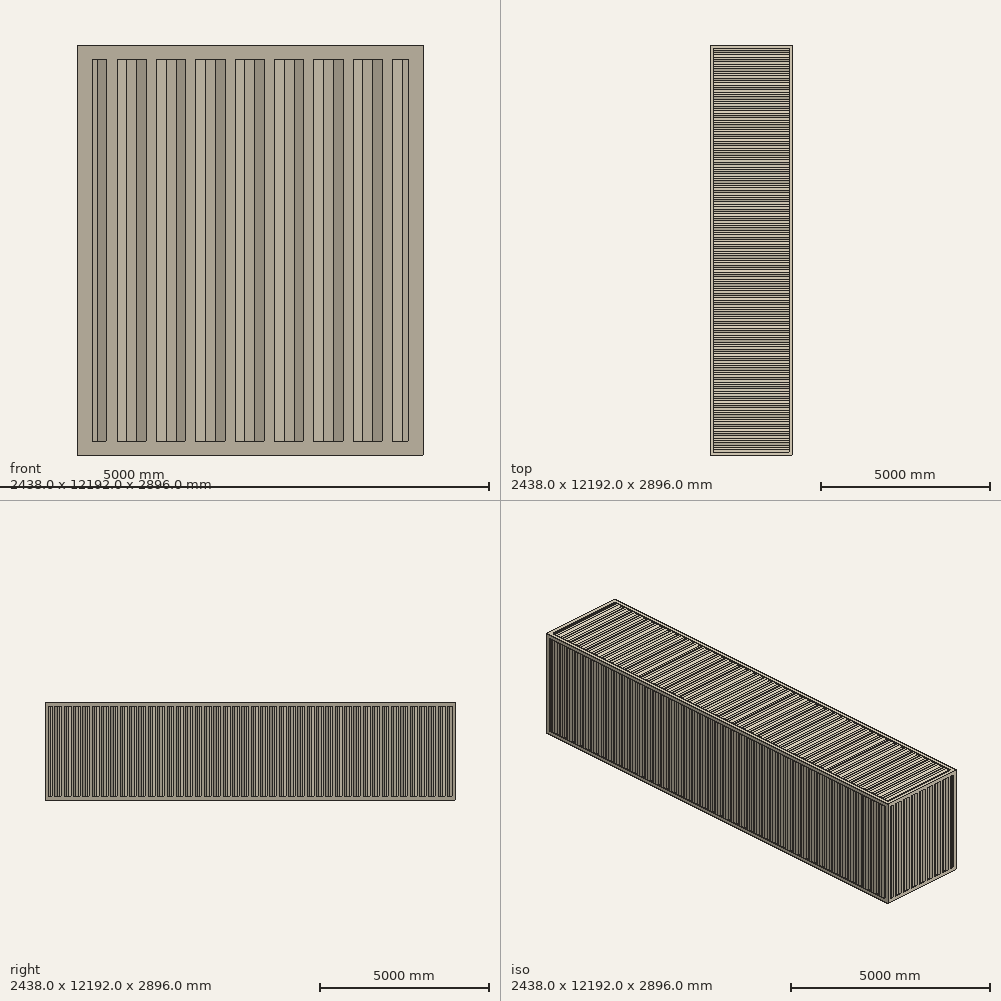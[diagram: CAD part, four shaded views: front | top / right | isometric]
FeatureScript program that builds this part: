
annotation { "Feature Type Name" : "Feature", "Feature Type Description" : "" }
export const myFeature = defineFeature(function(context is Context, id is Id, definition is map)
    precondition{}
    {
        {
            var Q0;
            Q0=qCreatedBy(makeId("Top.planeOp"),FACE);
            var sketch = newSketch(context, id + "F0", { "sketchPlane" : qUnion([Q0])});
            skLineSegment(sketch, "E0.bottom", {"start": v(0, 0) * mm, "end": v(-2438, 0) * mm});
            skLineSegment(sketch, "E0.top", {"start": v(0, 12192) * mm, "end": v(-2438, 12192) * mm});
            skLineSegment(sketch, "E0.left", {"start": v(0, 0) * mm, "end": v(0, 12192) * mm});
            skLineSegment(sketch, "E0.right", {"start": v(-2438, 0) * mm, "end": v(-2438, 12192) * mm});
            skSolve(sketch);
        }
        {
            var Q0;
            Q0 = qSketchRegion(id + "F0", true);
            extrude(context, id + "F1", {"entities" : qUnion([Q0]), "depth" : 2896 * mm, "offsetDistance" : 25 * mm});
        }
        {
            var Q0;
            Q0=makeQuery(id+"F1.opExtrude","SWEPT_FACE",FACE,{"disambiguationData":[OSD([sQuery(id+"F0.wireOp",EDGE,"E0.bottom")])]});
            var sketch = newSketch(context, id + "F2", { "sketchPlane" : qUnion([Q0])});
            skLineSegment(sketch, "E1", {"start": v(-2438, 2896) * mm, "end": v(-2338, 2896) * mm});
            skLineSegment(sketch, "E2", {"start": v(-2338, 2896) * mm, "end": v(-2338, 100) * mm});
            skLineSegment(sketch, "E3", {"start": v(-2338, 100) * mm, "end": v(-100, 100) * mm});
            skLineSegment(sketch, "E4", {"start": v(-100, 100) * mm, "end": v(-100, 2796) * mm});
            skLineSegment(sketch, "E5", {"start": v(-100, 2796) * mm, "end": v(-2338, 2796) * mm});
            skSolve(sketch);
        }
        {
            var Q0;
            Q0 = qSketchRegion(id + "F2", true);
            extrude(context, id + "F3", {"entities" : qUnion([Q0]), "operationType" : NewBodyOperationType.REMOVE, "oppositeDirection" : true, "depth" : 12192 * mm, "offsetDistance" : 25 * mm});
        }
        {
            var Q0;
            Q0=makeQuery(id+"F1.opExtrude","SWEPT_FACE",FACE,{"disambiguationData":[OSD([sQuery(id+"F0.wireOp",EDGE,"E0.left")])]});
            var sketch = newSketch(context, id + "F4", { "sketchPlane" : qUnion([Q0])});
            skLineSegment(sketch, "E6", {"start": v(0, 2896) * mm, "end": v(100, 2896) * mm});
            skLineSegment(sketch, "E7", {"start": v(100, 2896) * mm, "end": v(100, 100) * mm});
            skLineSegment(sketch, "E8", {"start": v(100, 100) * mm, "end": v(12092, 100) * mm});
            skLineSegment(sketch, "E9", {"start": v(12092, 100) * mm, "end": v(12092, 2796) * mm});
            skLineSegment(sketch, "E10", {"start": v(12092, 2796) * mm, "end": v(100, 2796) * mm});
            skSolve(sketch);
        }
        {
            var Q0;
            Q0 = qSketchRegion(id + "F4", true);
            extrude(context, id + "F5", {"entities" : qUnion([Q0]), "operationType" : NewBodyOperationType.REMOVE, "oppositeDirection" : true, "depth" : 2438 * mm, "offsetDistance" : 25 * mm});
        }
        {
            var Q0;
            Q0=makeQuery(id+"F1.opExtrude","CAP_FACE",FACE,{"disambiguationData":[OSD([sQuery(id+"F0.wireOp",EDGE,"E0.bottom"),sQuery(id+"F0.wireOp",EDGE,"E0.top"),sQuery(id+"F0.wireOp",EDGE,"E0.left"),sQuery(id+"F0.wireOp",EDGE,"E0.right")])],"isStart":false});
            var sketch = newSketch(context, id + "F6", { "sketchPlane" : qUnion([Q0])});
            skLineSegment(sketch, "E11", {"start": v(-2438, 0) * mm, "end": v(-2338, 0) * mm});
            skLineSegment(sketch, "E12", {"start": v(-2338, 0) * mm, "end": v(-2338, 12092) * mm});
            skLineSegment(sketch, "E13", {"start": v(-2338, 12092) * mm, "end": v(-100, 12092) * mm});
            skLineSegment(sketch, "E14", {"start": v(-100, 12092) * mm, "end": v(-100, 100) * mm});
            skLineSegment(sketch, "E15", {"start": v(-100, 100) * mm, "end": v(-2338, 100) * mm});
            skSolve(sketch);
        }
        {
            var Q0;
            Q0 = qSketchRegion(id + "F6", true);
            extrude(context, id + "F7", {"entities" : qUnion([Q0]), "operationType" : NewBodyOperationType.REMOVE, "oppositeDirection" : true, "depth" : 100 * mm, "offsetDistance" : 25 * mm});
        }
        {
            var Q0;
            Q0=makeQuery(id+"F5.boolean.opBoolean","MERGE",FACE,{"derivedFrom":[makeQuery(id+"F3.boolean.opBoolean","COPY",FACE,{"derivedFrom":makeQuery(id+"F3.opExtrude","SWEPT_FACE",FACE,{"disambiguationData":[OSD([sQuery(id+"F2.wireOp",EDGE,"E3")])]})})],"fromTools":[makeQuery(id+"F5.opExtrude","SWEPT_FACE",FACE,{"disambiguationData":[OSD([sQuery(id+"F4.wireOp",EDGE,"E8")])]})]});
            var sketch = newSketch(context, id + "F8", { "sketchPlane" : qUnion([Q0])});
            skLineSegment(sketch, "E16", {"start": v(-2338, 36) * mm, "end": v(-2301, 36) * mm});
            skLineSegment(sketch, "E17", {"start": v(-2233, 0) * mm, "end": v(-2161, 0) * mm});
            skLineSegment(sketch, "E18", {"start": v(-2093, 36) * mm, "end": v(-2023, 36) * mm});
            skLineSegment(sketch, "E19", {"start": v(-2301, 36) * mm, "end": v(-2233, 0) * mm});
            skLineSegment(sketch, "E20", {"start": v(-2161, 0) * mm, "end": v(-2093, 36) * mm});
            skLineSegment(sketch, "E21.1.0.0", {"start": v(-2023, 36) * mm, "end": v(-1955, 0) * mm});
            skLineSegment(sketch, "E21.1.0.1", {"start": v(-1955, 0) * mm, "end": v(-1883, 0) * mm});
            skLineSegment(sketch, "E21.1.0.2", {"start": v(-1883, 0) * mm, "end": v(-1815, 36) * mm});
            skLineSegment(sketch, "E21.1.0.3", {"start": v(-1815, 36) * mm, "end": v(-1745, 36) * mm});
            skLineSegment(sketch, "E21.2.0.0", {"start": v(-1745, 36) * mm, "end": v(-1677, 0) * mm});
            skLineSegment(sketch, "E21.2.0.1", {"start": v(-1677, 0) * mm, "end": v(-1605, 0) * mm});
            skLineSegment(sketch, "E21.2.0.2", {"start": v(-1605, 0) * mm, "end": v(-1537, 36) * mm});
            skLineSegment(sketch, "E21.2.0.3", {"start": v(-1537, 36) * mm, "end": v(-1467, 36) * mm});
            skLineSegment(sketch, "E21.3.0.0", {"start": v(-1467, 36) * mm, "end": v(-1399, 0) * mm});
            skLineSegment(sketch, "E21.3.0.1", {"start": v(-1399, 0) * mm, "end": v(-1327, 0) * mm});
            skLineSegment(sketch, "E21.3.0.2", {"start": v(-1327, 0) * mm, "end": v(-1259, 36) * mm});
            skLineSegment(sketch, "E21.3.0.3", {"start": v(-1259, 36) * mm, "end": v(-1189, 36) * mm});
            skLineSegment(sketch, "E21.4.0.0", {"start": v(-1189, 36) * mm, "end": v(-1121, 0) * mm});
            skLineSegment(sketch, "E21.4.0.1", {"start": v(-1121, 0) * mm, "end": v(-1049, 0) * mm});
            skLineSegment(sketch, "E21.4.0.2", {"start": v(-1049, 0) * mm, "end": v(-981, 36) * mm});
            skLineSegment(sketch, "E21.4.0.3", {"start": v(-981, 36) * mm, "end": v(-911, 36) * mm});
            skLineSegment(sketch, "E21.5.0.0", {"start": v(-911, 36) * mm, "end": v(-843, 0) * mm});
            skLineSegment(sketch, "E21.5.0.1", {"start": v(-843, 0) * mm, "end": v(-771, 0) * mm});
            skLineSegment(sketch, "E21.5.0.2", {"start": v(-771, 0) * mm, "end": v(-703, 36) * mm});
            skLineSegment(sketch, "E21.5.0.3", {"start": v(-703, 36) * mm, "end": v(-633, 36) * mm});
            skLineSegment(sketch, "E21.6.0.0", {"start": v(-633, 36) * mm, "end": v(-565, 0) * mm});
            skLineSegment(sketch, "E21.6.0.1", {"start": v(-565, 0) * mm, "end": v(-493, 0) * mm});
            skLineSegment(sketch, "E21.6.0.2", {"start": v(-493, 0) * mm, "end": v(-425, 36) * mm});
            skLineSegment(sketch, "E21.6.0.3", {"start": v(-425, 36) * mm, "end": v(-355, 36) * mm});
            skLineSegment(sketch, "E21.direction1", {"start": v(-2301, 36) * mm, "end": v(-2023, 36) * mm, "construction": true});
            skLineSegment(sketch, "E22.1.0.0", {"start": v(-355, 36) * mm, "end": v(-287, 0) * mm});
            skLineSegment(sketch, "E22.1.0.1", {"start": v(-287, 0) * mm, "end": v(-215, 0) * mm});
            skLineSegment(sketch, "E22.1.0.2", {"start": v(-215, 0) * mm, "end": v(-147, 36) * mm});
            skLineSegment(sketch, "E22.direction1", {"start": v(-633, 36) * mm, "end": v(-355, 36) * mm, "construction": true});
            skLineSegment(sketch, "E23", {"start": v(-147, 36) * mm, "end": v(-100, 36) * mm});
            skLineSegment(sketch, "E24.0.1.0", {"start": v(-2301, 37) * mm, "end": v(-2023, 37) * mm, "construction": true});
            skLineSegment(sketch, "E24.0.1.1", {"start": v(-633, 37) * mm, "end": v(-355, 37) * mm, "construction": true});
            skLineSegment(sketch, "E24.0.1.2", {"start": v(-355, 37) * mm, "end": v(-287, 1) * mm});
            skLineSegment(sketch, "E24.0.1.3", {"start": v(-1259, 37) * mm, "end": v(-1189, 37) * mm});
            skLineSegment(sketch, "E24.0.1.4", {"start": v(-147, 37) * mm, "end": v(-100, 37) * mm});
            skLineSegment(sketch, "E24.0.1.5", {"start": v(-1605, 1) * mm, "end": v(-1537, 37) * mm});
            skLineSegment(sketch, "E24.0.1.6", {"start": v(-1467, 37) * mm, "end": v(-1399, 1) * mm});
            skLineSegment(sketch, "E24.0.1.7", {"start": v(-1049, 1) * mm, "end": v(-981, 37) * mm});
            skLineSegment(sketch, "E24.0.1.8", {"start": v(-633, 37) * mm, "end": v(-565, 1) * mm});
            skLineSegment(sketch, "E24.0.1.9", {"start": v(-1955, 1) * mm, "end": v(-1883, 1) * mm});
            skLineSegment(sketch, "E24.0.1.10", {"start": v(-215, 1) * mm, "end": v(-147, 37) * mm});
            skLineSegment(sketch, "E24.0.1.11", {"start": v(-911, 37) * mm, "end": v(-843, 1) * mm});
            skLineSegment(sketch, "E24.0.1.12", {"start": v(-1883, 1) * mm, "end": v(-1815, 37) * mm});
            skLineSegment(sketch, "E24.0.1.13", {"start": v(-2023, 37) * mm, "end": v(-1955, 1) * mm});
            skLineSegment(sketch, "E24.0.1.14", {"start": v(-493, 1) * mm, "end": v(-425, 37) * mm});
            skLineSegment(sketch, "E24.0.1.15", {"start": v(-1677, 1) * mm, "end": v(-1605, 1) * mm});
            skLineSegment(sketch, "E24.0.1.16", {"start": v(-1189, 37) * mm, "end": v(-1121, 1) * mm});
            skLineSegment(sketch, "E24.0.1.17", {"start": v(-1745, 37) * mm, "end": v(-1677, 1) * mm});
            skLineSegment(sketch, "E24.0.1.18", {"start": v(-287, 1) * mm, "end": v(-215, 1) * mm});
            skLineSegment(sketch, "E24.0.1.19", {"start": v(-981, 37) * mm, "end": v(-911, 37) * mm});
            skLineSegment(sketch, "E24.0.1.20", {"start": v(-843, 1) * mm, "end": v(-771, 1) * mm});
            skLineSegment(sketch, "E24.0.1.21", {"start": v(-771, 1) * mm, "end": v(-703, 37) * mm});
            skLineSegment(sketch, "E24.0.1.22", {"start": v(-1815, 37) * mm, "end": v(-1745, 37) * mm});
            skLineSegment(sketch, "E24.0.1.23", {"start": v(-565, 1) * mm, "end": v(-493, 1) * mm});
            skLineSegment(sketch, "E24.0.1.24", {"start": v(-2161, 1) * mm, "end": v(-2093, 37) * mm});
            skLineSegment(sketch, "E24.0.1.25", {"start": v(-1121, 1) * mm, "end": v(-1049, 1) * mm});
            skLineSegment(sketch, "E24.0.1.26", {"start": v(-2301, 37) * mm, "end": v(-2233, 1) * mm});
            skLineSegment(sketch, "E24.0.1.27", {"start": v(-1537, 37) * mm, "end": v(-1467, 37) * mm});
            skLineSegment(sketch, "E24.0.1.28", {"start": v(-1399, 1) * mm, "end": v(-1327, 1) * mm});
            skLineSegment(sketch, "E24.0.1.29", {"start": v(-2233, 1) * mm, "end": v(-2161, 1) * mm});
            skLineSegment(sketch, "E24.0.1.30", {"start": v(-1327, 1) * mm, "end": v(-1259, 37) * mm});
            skLineSegment(sketch, "E24.0.1.31", {"start": v(-425, 37) * mm, "end": v(-355, 37) * mm});
            skLineSegment(sketch, "E24.0.1.32", {"start": v(-2093, 37) * mm, "end": v(-2023, 37) * mm});
            skLineSegment(sketch, "E24.0.1.33", {"start": v(-703, 37) * mm, "end": v(-633, 37) * mm});
            skLineSegment(sketch, "E24.0.1.34", {"start": v(-2338, 37) * mm, "end": v(-2301, 37) * mm});
            skLineSegment(sketch, "E24.direction1", {"start": v(-2338, 36) * mm, "end": v(-2313, 36) * mm, "construction": true});
            skLineSegment(sketch, "E24.direction2", {"start": v(-2338, 36) * mm, "end": v(-2338, 37) * mm, "construction": true});
            skLineSegment(sketch, "E25", {"start": v(-2338, 37) * mm, "end": v(-2338, 36) * mm});
            skLineSegment(sketch, "E26", {"start": v(-100, 37) * mm, "end": v(-100, 36) * mm});
            skSolve(sketch);
        }
        {
            var Q0;
            Q0 = qSketchRegion(id + "F8", true);
            extrude(context, id + "F9", {"entities" : qUnion([Q0]), "operationType" : NewBodyOperationType.ADD, "depth" : 2696 * mm, "offsetDistance" : 25 * mm});
        }
        {
            var Q0;
            {var subQ4=makeQuery(id+"F3.boolean.opBoolean","COPY",FACE,{"derivedFrom":makeQuery(id+"F3.opExtrude","SWEPT_FACE",FACE,{"disambiguationData":[OSD([sQuery(id+"F2.wireOp",EDGE,"E3")])]})});var subQ5=makeQuery(id+"F5.opExtrude","SWEPT_FACE",FACE,{"disambiguationData":[OSD([sQuery(id+"F4.wireOp",EDGE,"E8")])]});Q0=makeQuery(id+"F9.boolean.opBoolean","SPLIT",FACE,{"disambiguationData":[TD([makeQuery(id+"F1.opExtrude","SWEPT_FACE",FACE,{"disambiguationData":[OSD([sQuery(id+"F0.wireOp",EDGE,"E0.top")])]})])],"derivedFrom":makeQuery(id+"F5.boolean.opBoolean","MERGE",FACE,{"derivedFrom":[subQ4],"fromTools":[subQ5]})});}
            var sketch = newSketch(context, id + "F10", { "sketchPlane" : qUnion([Q0])});
            skLineSegment(sketch, "E27", {"start": v(-100, 12156) * mm, "end": v(-137, 12156) * mm});
            skLineSegment(sketch, "E28", {"start": v(-205.08, 12191.96) * mm, "end": v(-277.08, 12191.96) * mm});
            skLineSegment(sketch, "E29", {"start": v(-345, 12156) * mm, "end": v(-415, 12156) * mm});
            skLineSegment(sketch, "E30", {"start": v(-137, 12156) * mm, "end": v(-205.08, 12191.96) * mm});
            skLineSegment(sketch, "E31", {"start": v(-277.08, 12191.96) * mm, "end": v(-345, 12156) * mm});
            skLineSegment(sketch, "E32.1.0.0", {"start": v(-415, 12156) * mm, "end": v(-483.08, 12191.96) * mm});
            skLineSegment(sketch, "E32.1.0.1", {"start": v(-483.08, 12191.96) * mm, "end": v(-555.08, 12191.96) * mm});
            skLineSegment(sketch, "E32.1.0.2", {"start": v(-555.08, 12191.96) * mm, "end": v(-623, 12156) * mm});
            skLineSegment(sketch, "E32.1.0.3", {"start": v(-623, 12156) * mm, "end": v(-693, 12156) * mm});
            skLineSegment(sketch, "E32.2.0.0", {"start": v(-693, 12156) * mm, "end": v(-761.08, 12191.96) * mm});
            skLineSegment(sketch, "E32.2.0.1", {"start": v(-761.08, 12191.96) * mm, "end": v(-833.08, 12191.96) * mm});
            skLineSegment(sketch, "E32.2.0.2", {"start": v(-833.08, 12191.96) * mm, "end": v(-901, 12156) * mm});
            skLineSegment(sketch, "E32.2.0.3", {"start": v(-901, 12156) * mm, "end": v(-971, 12156) * mm});
            skLineSegment(sketch, "E32.3.0.0", {"start": v(-971, 12156) * mm, "end": v(-1039.08, 12191.96) * mm});
            skLineSegment(sketch, "E32.3.0.1", {"start": v(-1039.08, 12191.96) * mm, "end": v(-1111.08, 12191.96) * mm});
            skLineSegment(sketch, "E32.3.0.2", {"start": v(-1111.08, 12191.96) * mm, "end": v(-1179, 12156) * mm});
            skLineSegment(sketch, "E32.3.0.3", {"start": v(-1179, 12156) * mm, "end": v(-1249, 12156) * mm});
            skLineSegment(sketch, "E32.4.0.0", {"start": v(-1249, 12156) * mm, "end": v(-1317.08, 12191.96) * mm});
            skLineSegment(sketch, "E32.4.0.1", {"start": v(-1317.08, 12191.96) * mm, "end": v(-1389.08, 12191.96) * mm});
            skLineSegment(sketch, "E32.4.0.2", {"start": v(-1389.08, 12191.96) * mm, "end": v(-1457, 12156) * mm});
            skLineSegment(sketch, "E32.4.0.3", {"start": v(-1457, 12156) * mm, "end": v(-1527, 12156) * mm});
            skLineSegment(sketch, "E32.5.0.0", {"start": v(-1527, 12156) * mm, "end": v(-1595.08, 12191.96) * mm});
            skLineSegment(sketch, "E32.5.0.1", {"start": v(-1595.08, 12191.96) * mm, "end": v(-1667.08, 12191.96) * mm});
            skLineSegment(sketch, "E32.5.0.2", {"start": v(-1667.08, 12191.96) * mm, "end": v(-1735, 12156) * mm});
            skLineSegment(sketch, "E32.5.0.3", {"start": v(-1735, 12156) * mm, "end": v(-1805, 12156) * mm});
            skLineSegment(sketch, "E32.6.0.0", {"start": v(-1805, 12156) * mm, "end": v(-1873.08, 12191.96) * mm});
            skLineSegment(sketch, "E32.6.0.1", {"start": v(-1873.08, 12191.96) * mm, "end": v(-1945.08, 12191.96) * mm});
            skLineSegment(sketch, "E32.6.0.2", {"start": v(-1945.08, 12191.96) * mm, "end": v(-2013, 12156) * mm});
            skLineSegment(sketch, "E32.6.0.3", {"start": v(-2013, 12156) * mm, "end": v(-2083, 12156) * mm});
            skLineSegment(sketch, "E32.direction1", {"start": v(-137, 12156) * mm, "end": v(-415, 12156) * mm, "construction": true});
            skLineSegment(sketch, "E33.1.0.0", {"start": v(-2083, 12156) * mm, "end": v(-2151.08, 12191.96) * mm});
            skLineSegment(sketch, "E33.1.0.1", {"start": v(-2151.08, 12191.96) * mm, "end": v(-2223.08, 12191.96) * mm});
            skLineSegment(sketch, "E33.1.0.2", {"start": v(-2223.08, 12191.96) * mm, "end": v(-2291, 12156) * mm});
            skLineSegment(sketch, "E33.direction1", {"start": v(-1805, 12156) * mm, "end": v(-2083, 12156) * mm, "construction": true});
            skLineSegment(sketch, "E34", {"start": v(-2291, 12156) * mm, "end": v(-2338, 12156) * mm});
            skLineSegment(sketch, "E35.0.1.0", {"start": v(-137, 12155) * mm, "end": v(-415, 12155) * mm, "construction": true});
            skLineSegment(sketch, "E35.0.1.1", {"start": v(-1805, 12155) * mm, "end": v(-2083, 12155) * mm, "construction": true});
            skLineSegment(sketch, "E35.0.1.2", {"start": v(-2083, 12155) * mm, "end": v(-2151.08, 12190.96) * mm});
            skLineSegment(sketch, "E35.0.1.3", {"start": v(-1179, 12155) * mm, "end": v(-1249, 12155) * mm});
            skLineSegment(sketch, "E35.0.1.4", {"start": v(-2291, 12155) * mm, "end": v(-2338, 12155) * mm});
            skLineSegment(sketch, "E35.0.1.5", {"start": v(-833.08, 12190.96) * mm, "end": v(-901, 12155) * mm});
            skLineSegment(sketch, "E35.0.1.6", {"start": v(-971, 12155) * mm, "end": v(-1039.08, 12190.96) * mm});
            skLineSegment(sketch, "E35.0.1.7", {"start": v(-1389.08, 12190.96) * mm, "end": v(-1457, 12155) * mm});
            skLineSegment(sketch, "E35.0.1.8", {"start": v(-1805, 12155) * mm, "end": v(-1873.08, 12190.96) * mm});
            skLineSegment(sketch, "E35.0.1.9", {"start": v(-483.08, 12190.96) * mm, "end": v(-555.08, 12190.96) * mm});
            skLineSegment(sketch, "E35.0.1.10", {"start": v(-2223.08, 12190.96) * mm, "end": v(-2291, 12155) * mm});
            skLineSegment(sketch, "E35.0.1.11", {"start": v(-1527, 12155) * mm, "end": v(-1595.08, 12190.96) * mm});
            skLineSegment(sketch, "E35.0.1.12", {"start": v(-555.08, 12190.96) * mm, "end": v(-623, 12155) * mm});
            skLineSegment(sketch, "E35.0.1.13", {"start": v(-415, 12155) * mm, "end": v(-483.08, 12190.96) * mm});
            skLineSegment(sketch, "E35.0.1.14", {"start": v(-1945.08, 12190.96) * mm, "end": v(-2013, 12155) * mm});
            skLineSegment(sketch, "E35.0.1.15", {"start": v(-761.08, 12190.96) * mm, "end": v(-833.08, 12190.96) * mm});
            skLineSegment(sketch, "E35.0.1.16", {"start": v(-1249, 12155) * mm, "end": v(-1317.08, 12190.96) * mm});
            skLineSegment(sketch, "E35.0.1.17", {"start": v(-693, 12155) * mm, "end": v(-761.08, 12190.96) * mm});
            skLineSegment(sketch, "E35.0.1.18", {"start": v(-2151.08, 12190.96) * mm, "end": v(-2223.08, 12190.96) * mm});
            skLineSegment(sketch, "E35.0.1.19", {"start": v(-1457, 12155) * mm, "end": v(-1527, 12155) * mm});
            skLineSegment(sketch, "E35.0.1.20", {"start": v(-1595.08, 12190.96) * mm, "end": v(-1667.08, 12190.96) * mm});
            skLineSegment(sketch, "E35.0.1.21", {"start": v(-1667.08, 12190.96) * mm, "end": v(-1735, 12155) * mm});
            skLineSegment(sketch, "E35.0.1.22", {"start": v(-623, 12155) * mm, "end": v(-693, 12155) * mm});
            skLineSegment(sketch, "E35.0.1.23", {"start": v(-1873.08, 12190.96) * mm, "end": v(-1945.08, 12190.96) * mm});
            skLineSegment(sketch, "E35.0.1.24", {"start": v(-277.08, 12190.96) * mm, "end": v(-345, 12155) * mm});
            skLineSegment(sketch, "E35.0.1.25", {"start": v(-1317.08, 12190.96) * mm, "end": v(-1389.08, 12190.96) * mm});
            skLineSegment(sketch, "E35.0.1.26", {"start": v(-137, 12155) * mm, "end": v(-205.08, 12190.96) * mm});
            skLineSegment(sketch, "E35.0.1.27", {"start": v(-901, 12155) * mm, "end": v(-971, 12155) * mm});
            skLineSegment(sketch, "E35.0.1.28", {"start": v(-1039.08, 12190.96) * mm, "end": v(-1111.08, 12190.96) * mm});
            skLineSegment(sketch, "E35.0.1.29", {"start": v(-205.08, 12190.96) * mm, "end": v(-277.08, 12190.96) * mm});
            skLineSegment(sketch, "E35.0.1.30", {"start": v(-1111.08, 12190.96) * mm, "end": v(-1179, 12155) * mm});
            skLineSegment(sketch, "E35.0.1.31", {"start": v(-2013, 12155) * mm, "end": v(-2083, 12155) * mm});
            skLineSegment(sketch, "E35.0.1.32", {"start": v(-345, 12155) * mm, "end": v(-415, 12155) * mm});
            skLineSegment(sketch, "E35.0.1.33", {"start": v(-1735, 12155) * mm, "end": v(-1805, 12155) * mm});
            skLineSegment(sketch, "E35.0.1.34", {"start": v(-100, 12155) * mm, "end": v(-137, 12155) * mm});
            skLineSegment(sketch, "E35.direction1", {"start": v(-100, 12156) * mm, "end": v(-125, 12156) * mm, "construction": true});
            skLineSegment(sketch, "E35.direction2", {"start": v(-100, 12156) * mm, "end": v(-100, 12155) * mm, "construction": true});
            skLineSegment(sketch, "E36", {"start": v(-100, 12156) * mm, "end": v(-100, 12155) * mm});
            skLineSegment(sketch, "E37", {"start": v(-2338, 12156) * mm, "end": v(-2338, 12155) * mm});
            skSolve(sketch);
        }
        {
            var Q0;
            Q0 = qSketchRegion(id + "F10", true);
            extrude(context, id + "F11", {"entities" : qUnion([Q0]), "operationType" : NewBodyOperationType.ADD, "depth" : 2696 * mm, "offsetDistance" : 25 * mm});
        }
        {
            var Q0;
            {var subQ5=makeQuery(id+"F3.boolean.opBoolean","COPY",FACE,{"derivedFrom":makeQuery(id+"F3.opExtrude","SWEPT_FACE",FACE,{"disambiguationData":[OSD([sQuery(id+"F2.wireOp",EDGE,"E3")])]})});var subQ6=makeQuery(id+"F5.opExtrude","SWEPT_FACE",FACE,{"disambiguationData":[OSD([sQuery(id+"F4.wireOp",EDGE,"E8")])]});var subQ12=makeQuery(id+"F1.opExtrude","SWEPT_FACE",FACE,{"disambiguationData":[OSD([sQuery(id+"F0.wireOp",EDGE,"E0.left")])]});Q0=makeQuery(id+"F11.boolean.opBoolean","SPLIT",FACE,{"disambiguationData":[TD([subQ12])],"derivedFrom":makeQuery(id+"F9.boolean.opBoolean","SPLIT",FACE,{"disambiguationData":[TD([makeQuery(id+"F1.opExtrude","SWEPT_FACE",FACE,{"disambiguationData":[OSD([sQuery(id+"F0.wireOp",EDGE,"E0.top")])]})])],"derivedFrom":makeQuery(id+"F5.boolean.opBoolean","MERGE",FACE,{"derivedFrom":[subQ5],"fromTools":[subQ6]})})});}
            var sketch = newSketch(context, id + "F12", { "sketchPlane" : qUnion([Q0])});
            skLineSegment(sketch, "E38", {"start": v(0, 100) * mm, "end": v(-36, 100) * mm});
            skLineSegment(sketch, "E39", {"start": v(-36, 100.17) * mm, "end": v(-36, 137.17) * mm});
            skLineSegment(sketch, "E40", {"start": v(0, 205.17) * mm, "end": v(0, 277.17) * mm});
            skLineSegment(sketch, "E41", {"start": v(-36, 345.17) * mm, "end": v(-36, 415.17) * mm});
            skLineSegment(sketch, "E42", {"start": v(-36, 137.17) * mm, "end": v(0, 205.17) * mm});
            skLineSegment(sketch, "E43", {"start": v(0, 277.17) * mm, "end": v(-36, 345.17) * mm});
            skLineSegment(sketch, "E44.1.0.0", {"start": v(-36, 415.17) * mm, "end": v(0, 483.17) * mm});
            skLineSegment(sketch, "E44.1.0.1", {"start": v(0, 483.17) * mm, "end": v(0, 555.17) * mm});
            skLineSegment(sketch, "E44.1.0.2", {"start": v(0, 555.17) * mm, "end": v(-36, 623.17) * mm});
            skLineSegment(sketch, "E44.1.0.3", {"start": v(-36, 623.17) * mm, "end": v(-36, 693.17) * mm});
            skLineSegment(sketch, "E44.2.0.0", {"start": v(-36, 693.17) * mm, "end": v(0, 761.17) * mm});
            skLineSegment(sketch, "E44.2.0.1", {"start": v(0, 761.17) * mm, "end": v(0, 833.17) * mm});
            skLineSegment(sketch, "E44.2.0.2", {"start": v(0, 833.17) * mm, "end": v(-36, 901.17) * mm});
            skLineSegment(sketch, "E44.2.0.3", {"start": v(-36, 901.17) * mm, "end": v(-36, 971.17) * mm});
            skLineSegment(sketch, "E44.3.0.0", {"start": v(-36, 971.17) * mm, "end": v(0, 1039.17) * mm});
            skLineSegment(sketch, "E44.3.0.1", {"start": v(0, 1039.17) * mm, "end": v(0, 1111.17) * mm});
            skLineSegment(sketch, "E44.3.0.2", {"start": v(0, 1111.17) * mm, "end": v(-36, 1179.17) * mm});
            skLineSegment(sketch, "E44.3.0.3", {"start": v(-36, 1179.17) * mm, "end": v(-36, 1249.17) * mm});
            skLineSegment(sketch, "E44.4.0.0", {"start": v(-36, 1249.17) * mm, "end": v(0, 1317.17) * mm});
            skLineSegment(sketch, "E44.4.0.1", {"start": v(0, 1317.17) * mm, "end": v(0, 1389.17) * mm});
            skLineSegment(sketch, "E44.4.0.2", {"start": v(0, 1389.17) * mm, "end": v(-36, 1457.17) * mm});
            skLineSegment(sketch, "E44.4.0.3", {"start": v(-36, 1457.17) * mm, "end": v(-36, 1527.17) * mm});
            skLineSegment(sketch, "E44.5.0.0", {"start": v(-36, 1527.17) * mm, "end": v(0, 1595.17) * mm});
            skLineSegment(sketch, "E44.5.0.1", {"start": v(0, 1595.17) * mm, "end": v(0, 1667.17) * mm});
            skLineSegment(sketch, "E44.5.0.2", {"start": v(0, 1667.17) * mm, "end": v(-36, 1735.17) * mm});
            skLineSegment(sketch, "E44.5.0.3", {"start": v(-36, 1735.17) * mm, "end": v(-36, 1805.17) * mm});
            skLineSegment(sketch, "E44.6.0.0", {"start": v(-36, 1805.17) * mm, "end": v(0, 1873.17) * mm});
            skLineSegment(sketch, "E44.6.0.1", {"start": v(0, 1873.17) * mm, "end": v(0, 1945.17) * mm});
            skLineSegment(sketch, "E44.6.0.2", {"start": v(0, 1945.17) * mm, "end": v(-36, 2013.17) * mm});
            skLineSegment(sketch, "E44.6.0.3", {"start": v(-36, 2013.17) * mm, "end": v(-36, 2083.17) * mm});
            skLineSegment(sketch, "E44.direction1", {"start": v(-36, 137.17) * mm, "end": v(-36, 415.17) * mm, "construction": true});
            skLineSegment(sketch, "E45.1.0.0", {"start": v(-36, 2083.17) * mm, "end": v(0, 2151.17) * mm});
            skLineSegment(sketch, "E45.1.0.1", {"start": v(0, 2151.17) * mm, "end": v(0, 2223.17) * mm});
            skLineSegment(sketch, "E45.1.0.2", {"start": v(0, 2223.17) * mm, "end": v(-36, 2291.17) * mm});
            skLineSegment(sketch, "E45.direction1", {"start": v(-36, 1805.17) * mm, "end": v(-36, 2083.17) * mm, "construction": true});
            skLineSegment(sketch, "E46.0.1.0", {"start": v(-37, 137.17) * mm, "end": v(-37, 415.17) * mm, "construction": true});
            skLineSegment(sketch, "E46.0.1.1", {"start": v(-37, 1805.17) * mm, "end": v(-37, 2083.17) * mm, "construction": true});
            skLineSegment(sketch, "E46.0.1.2", {"start": v(-37, 2083.17) * mm, "end": v(-1, 2151.17) * mm});
            skLineSegment(sketch, "E46.0.1.3", {"start": v(-37, 1179.17) * mm, "end": v(-37, 1249.17) * mm});
            skLineSegment(sketch, "E46.0.1.5", {"start": v(-1, 833.17) * mm, "end": v(-37, 901.17) * mm});
            skLineSegment(sketch, "E46.0.1.6", {"start": v(-37, 971.17) * mm, "end": v(-1, 1039.17) * mm});
            skLineSegment(sketch, "E46.0.1.7", {"start": v(-1, 1389.17) * mm, "end": v(-37, 1457.17) * mm});
            skLineSegment(sketch, "E46.0.1.8", {"start": v(-37, 1805.17) * mm, "end": v(-1, 1873.17) * mm});
            skLineSegment(sketch, "E46.0.1.9", {"start": v(-1, 483.17) * mm, "end": v(-1, 555.17) * mm});
            skLineSegment(sketch, "E46.0.1.10", {"start": v(-1, 2223.17) * mm, "end": v(-37, 2291.17) * mm});
            skLineSegment(sketch, "E46.0.1.11", {"start": v(-37, 1527.17) * mm, "end": v(-1, 1595.17) * mm});
            skLineSegment(sketch, "E46.0.1.12", {"start": v(-1, 555.17) * mm, "end": v(-37, 623.17) * mm});
            skLineSegment(sketch, "E46.0.1.13", {"start": v(-37, 415.17) * mm, "end": v(-1, 483.17) * mm});
            skLineSegment(sketch, "E46.0.1.14", {"start": v(-1, 1945.17) * mm, "end": v(-37, 2013.17) * mm});
            skLineSegment(sketch, "E46.0.1.15", {"start": v(-1, 761.17) * mm, "end": v(-1, 833.17) * mm});
            skLineSegment(sketch, "E46.0.1.16", {"start": v(-37, 1249.17) * mm, "end": v(-1, 1317.17) * mm});
            skLineSegment(sketch, "E46.0.1.17", {"start": v(-37, 693.17) * mm, "end": v(-1, 761.17) * mm});
            skLineSegment(sketch, "E46.0.1.18", {"start": v(-1, 2151.17) * mm, "end": v(-1, 2223.17) * mm});
            skLineSegment(sketch, "E46.0.1.19", {"start": v(-37, 1457.17) * mm, "end": v(-37, 1527.17) * mm});
            skLineSegment(sketch, "E46.0.1.20", {"start": v(-1, 1595.17) * mm, "end": v(-1, 1667.17) * mm});
            skLineSegment(sketch, "E46.0.1.21", {"start": v(-1, 1667.17) * mm, "end": v(-37, 1735.17) * mm});
            skLineSegment(sketch, "E46.0.1.22", {"start": v(-37, 623.17) * mm, "end": v(-37, 693.17) * mm});
            skLineSegment(sketch, "E46.0.1.23", {"start": v(-1, 1873.17) * mm, "end": v(-1, 1945.17) * mm});
            skLineSegment(sketch, "E46.0.1.24", {"start": v(-1, 277.17) * mm, "end": v(-37, 345.17) * mm});
            skLineSegment(sketch, "E46.0.1.25", {"start": v(-1, 1317.17) * mm, "end": v(-1, 1389.17) * mm});
            skLineSegment(sketch, "E46.0.1.26", {"start": v(-37, 137.17) * mm, "end": v(-1, 205.17) * mm});
            skLineSegment(sketch, "E46.0.1.27", {"start": v(-37, 901.17) * mm, "end": v(-37, 971.17) * mm});
            skLineSegment(sketch, "E46.0.1.28", {"start": v(-1, 1039.17) * mm, "end": v(-1, 1111.17) * mm});
            skLineSegment(sketch, "E46.0.1.29", {"start": v(-1, 205.17) * mm, "end": v(-1, 277.17) * mm});
            skLineSegment(sketch, "E46.0.1.30", {"start": v(-1, 1111.17) * mm, "end": v(-37, 1179.17) * mm});
            skLineSegment(sketch, "E46.0.1.31", {"start": v(-37, 2013.17) * mm, "end": v(-37, 2083.17) * mm});
            skLineSegment(sketch, "E46.0.1.32", {"start": v(-37, 345.17) * mm, "end": v(-37, 415.17) * mm});
            skLineSegment(sketch, "E46.0.1.33", {"start": v(-37, 1735.17) * mm, "end": v(-37, 1805.17) * mm});
            skLineSegment(sketch, "E46.0.1.34", {"start": v(-37, 100.17) * mm, "end": v(-37, 137.17) * mm});
            skLineSegment(sketch, "E47", {"start": v(-37, 100.17) * mm, "end": v(-37, 100) * mm});
            skLineSegment(sketch, "E48", {"start": v(-37, 100) * mm, "end": v(-36, 100) * mm});
            skLineSegment(sketch, "E49", {"start": v(-36, 100) * mm, "end": v(-36, 100.17) * mm});
            skLineSegment(sketch, "E50.0.1.0", {"start": v(0, 2779.17) * mm, "end": v(-36, 2847.17) * mm});
            skLineSegment(sketch, "E50.0.1.1", {"start": v(-1, 2779.17) * mm, "end": v(-37, 2847.17) * mm});
            skLineSegment(sketch, "E50.0.1.2", {"start": v(0, 2707.17) * mm, "end": v(0, 2779.17) * mm});
            skLineSegment(sketch, "E50.0.1.3", {"start": v(0, 2429.17) * mm, "end": v(0, 2501.17) * mm});
            skLineSegment(sketch, "E50.0.1.4", {"start": v(-37, 2639.17) * mm, "end": v(-1, 2707.17) * mm});
            skLineSegment(sketch, "E50.0.1.5", {"start": v(-37, 2569.17) * mm, "end": v(-37, 2639.17) * mm});
            skLineSegment(sketch, "E50.0.1.6", {"start": v(-37, 2917.17) * mm, "end": v(-1, 2985.17) * mm});
            skLineSegment(sketch, "E50.0.1.7", {"start": v(-1, 2501.17) * mm, "end": v(-37, 2569.17) * mm});
            skLineSegment(sketch, "E50.0.1.8", {"start": v(-36, 2917.17) * mm, "end": v(0, 2985.17) * mm});
            skLineSegment(sketch, "E50.0.1.9", {"start": v(-36, 2569.17) * mm, "end": v(-36, 2639.17) * mm});
            skLineSegment(sketch, "E50.0.1.10", {"start": v(-37, 2291.17) * mm, "end": v(-37, 2361.17) * mm});
            skLineSegment(sketch, "E50.0.1.11", {"start": v(-36, 2847.17) * mm, "end": v(-36, 2917.17) * mm});
            skLineSegment(sketch, "E50.0.1.12", {"start": v(-1, 2707.17) * mm, "end": v(-1, 2779.17) * mm});
            skLineSegment(sketch, "E50.0.1.13", {"start": v(-37, 2361.17) * mm, "end": v(-1, 2429.17) * mm});
            skLineSegment(sketch, "E50.0.1.14", {"start": v(-36, 2361.17) * mm, "end": v(0, 2429.17) * mm});
            skLineSegment(sketch, "E50.0.1.15", {"start": v(0, 2985.17) * mm, "end": v(0, 3057.17) * mm});
            skLineSegment(sketch, "E50.0.1.16", {"start": v(0, 2501.17) * mm, "end": v(-36, 2569.17) * mm});
            skLineSegment(sketch, "E50.0.1.17", {"start": v(-36, 2291.17) * mm, "end": v(-36, 2361.17) * mm});
            skLineSegment(sketch, "E50.0.1.18", {"start": v(-1, 2429.17) * mm, "end": v(-1, 2501.17) * mm});
            skLineSegment(sketch, "E50.0.1.19", {"start": v(-36, 2639.17) * mm, "end": v(0, 2707.17) * mm});
            skLineSegment(sketch, "E50.0.1.20", {"start": v(-1, 2985.17) * mm, "end": v(-1, 3057.17) * mm});
            skLineSegment(sketch, "E50.0.1.21", {"start": v(-37, 2847.17) * mm, "end": v(-37, 2917.17) * mm});
            skLineSegment(sketch, "E50.0.1.22", {"start": v(-36, 3751.17) * mm, "end": v(-36, 4029.17) * mm, "construction": true});
            skLineSegment(sketch, "E50.0.1.23", {"start": v(0, 4169.17) * mm, "end": v(-36, 4237.17) * mm});
            skLineSegment(sketch, "E50.0.1.24", {"start": v(-1, 4169.17) * mm, "end": v(-37, 4237.17) * mm});
            skLineSegment(sketch, "E50.0.1.25", {"start": v(-37, 3751.17) * mm, "end": v(-37, 4029.17) * mm, "construction": true});
            skLineSegment(sketch, "E50.0.1.26", {"start": v(-1, 3335.17) * mm, "end": v(-37, 3403.17) * mm});
            skLineSegment(sketch, "E50.0.1.27", {"start": v(0, 3335.17) * mm, "end": v(-36, 3403.17) * mm});
            skLineSegment(sketch, "E50.0.1.28", {"start": v(0, 4097.17) * mm, "end": v(0, 4169.17) * mm});
            skLineSegment(sketch, "E50.0.1.29", {"start": v(-36, 4029.17) * mm, "end": v(0, 4097.17) * mm});
            skLineSegment(sketch, "E50.0.1.30", {"start": v(0, 3263.17) * mm, "end": v(0, 3335.17) * mm});
            skLineSegment(sketch, "E50.0.1.31", {"start": v(-1, 3263.17) * mm, "end": v(-1, 3335.17) * mm});
            skLineSegment(sketch, "E50.0.1.32", {"start": v(-37, 4029.17) * mm, "end": v(-1, 4097.17) * mm});
            skLineSegment(sketch, "E50.0.1.33", {"start": v(-1, 4097.17) * mm, "end": v(-1, 4169.17) * mm});
            skLineSegment(sketch, "E50.0.1.34", {"start": v(-37, 3681.17) * mm, "end": v(-37, 3751.17) * mm});
            skLineSegment(sketch, "E50.0.1.35", {"start": v(-1, 3541.17) * mm, "end": v(-1, 3613.17) * mm});
            skLineSegment(sketch, "E50.0.1.36", {"start": v(-37, 3125.17) * mm, "end": v(-37, 3195.17) * mm});
            skLineSegment(sketch, "E50.0.1.37", {"start": v(-1, 3891.17) * mm, "end": v(-37, 3959.17) * mm});
            skLineSegment(sketch, "E50.0.1.38", {"start": v(-36, 3473.17) * mm, "end": v(0, 3541.17) * mm});
            skLineSegment(sketch, "E50.0.1.39", {"start": v(-1, 3613.17) * mm, "end": v(-37, 3681.17) * mm});
            skLineSegment(sketch, "E50.0.1.40", {"start": v(0, 3819.17) * mm, "end": v(0, 3891.17) * mm});
            skLineSegment(sketch, "E50.0.1.41", {"start": v(-36, 3751.17) * mm, "end": v(0, 3819.17) * mm});
            skLineSegment(sketch, "E50.0.1.42", {"start": v(0, 3541.17) * mm, "end": v(0, 3613.17) * mm});
            skLineSegment(sketch, "E50.0.1.43", {"start": v(-36, 3125.17) * mm, "end": v(-36, 3195.17) * mm});
            skLineSegment(sketch, "E50.0.1.44", {"start": v(-37, 3473.17) * mm, "end": v(-1, 3541.17) * mm});
            skLineSegment(sketch, "E50.0.1.45", {"start": v(-37, 3195.17) * mm, "end": v(-1, 3263.17) * mm});
            skLineSegment(sketch, "E50.0.1.46", {"start": v(-1, 3057.17) * mm, "end": v(-37, 3125.17) * mm});
            skLineSegment(sketch, "E50.0.1.47", {"start": v(-1, 3819.17) * mm, "end": v(-1, 3891.17) * mm});
            skLineSegment(sketch, "E50.0.1.48", {"start": v(-37, 3403.17) * mm, "end": v(-37, 3473.17) * mm});
            skLineSegment(sketch, "E50.0.1.49", {"start": v(-37, 3959.17) * mm, "end": v(-37, 4029.17) * mm});
            skLineSegment(sketch, "E50.0.1.50", {"start": v(-36, 3403.17) * mm, "end": v(-36, 3473.17) * mm});
            skLineSegment(sketch, "E50.0.1.51", {"start": v(0, 3057.17) * mm, "end": v(-36, 3125.17) * mm});
            skLineSegment(sketch, "E50.0.1.52", {"start": v(-36, 3195.17) * mm, "end": v(0, 3263.17) * mm});
            skLineSegment(sketch, "E50.0.1.53", {"start": v(-36, 3959.17) * mm, "end": v(-36, 4029.17) * mm});
            skLineSegment(sketch, "E50.0.1.54", {"start": v(-36, 3681.17) * mm, "end": v(-36, 3751.17) * mm});
            skLineSegment(sketch, "E50.0.1.55", {"start": v(0, 3891.17) * mm, "end": v(-36, 3959.17) * mm});
            skLineSegment(sketch, "E50.0.1.56", {"start": v(0, 3613.17) * mm, "end": v(-36, 3681.17) * mm});
            skLineSegment(sketch, "E50.0.1.57", {"start": v(-37, 3751.17) * mm, "end": v(-1, 3819.17) * mm});
            skLineSegment(sketch, "E50.0.2.0", {"start": v(0, 4725.17) * mm, "end": v(-36, 4793.17) * mm});
            skLineSegment(sketch, "E50.0.2.1", {"start": v(-1, 4725.17) * mm, "end": v(-37, 4793.17) * mm});
            skLineSegment(sketch, "E50.0.2.2", {"start": v(0, 4653.17) * mm, "end": v(0, 4725.17) * mm});
            skLineSegment(sketch, "E50.0.2.3", {"start": v(0, 4375.17) * mm, "end": v(0, 4447.17) * mm});
            skLineSegment(sketch, "E50.0.2.4", {"start": v(-37, 4585.17) * mm, "end": v(-1, 4653.17) * mm});
            skLineSegment(sketch, "E50.0.2.5", {"start": v(-37, 4515.17) * mm, "end": v(-37, 4585.17) * mm});
            skLineSegment(sketch, "E50.0.2.6", {"start": v(-37, 4863.17) * mm, "end": v(-1, 4931.17) * mm});
            skLineSegment(sketch, "E50.0.2.7", {"start": v(-1, 4447.17) * mm, "end": v(-37, 4515.17) * mm});
            skLineSegment(sketch, "E50.0.2.8", {"start": v(-36, 4863.17) * mm, "end": v(0, 4931.17) * mm});
            skLineSegment(sketch, "E50.0.2.9", {"start": v(-36, 4515.17) * mm, "end": v(-36, 4585.17) * mm});
            skLineSegment(sketch, "E50.0.2.10", {"start": v(-37, 4237.17) * mm, "end": v(-37, 4307.17) * mm});
            skLineSegment(sketch, "E50.0.2.11", {"start": v(-36, 4793.17) * mm, "end": v(-36, 4863.17) * mm});
            skLineSegment(sketch, "E50.0.2.12", {"start": v(-1, 4653.17) * mm, "end": v(-1, 4725.17) * mm});
            skLineSegment(sketch, "E50.0.2.13", {"start": v(-37, 4307.17) * mm, "end": v(-1, 4375.17) * mm});
            skLineSegment(sketch, "E50.0.2.14", {"start": v(-36, 4307.17) * mm, "end": v(0, 4375.17) * mm});
            skLineSegment(sketch, "E50.0.2.15", {"start": v(0, 4931.17) * mm, "end": v(0, 5003.17) * mm});
            skLineSegment(sketch, "E50.0.2.16", {"start": v(0, 4447.17) * mm, "end": v(-36, 4515.17) * mm});
            skLineSegment(sketch, "E50.0.2.17", {"start": v(-36, 4237.17) * mm, "end": v(-36, 4307.17) * mm});
            skLineSegment(sketch, "E50.0.2.18", {"start": v(-1, 4375.17) * mm, "end": v(-1, 4447.17) * mm});
            skLineSegment(sketch, "E50.0.2.19", {"start": v(-36, 4585.17) * mm, "end": v(0, 4653.17) * mm});
            skLineSegment(sketch, "E50.0.2.20", {"start": v(-1, 4931.17) * mm, "end": v(-1, 5003.17) * mm});
            skLineSegment(sketch, "E50.0.2.21", {"start": v(-37, 4793.17) * mm, "end": v(-37, 4863.17) * mm});
            skLineSegment(sketch, "E50.0.2.22", {"start": v(-36, 5697.17) * mm, "end": v(-36, 5975.17) * mm, "construction": true});
            skLineSegment(sketch, "E50.0.2.23", {"start": v(0, 6115.17) * mm, "end": v(-36, 6183.17) * mm});
            skLineSegment(sketch, "E50.0.2.24", {"start": v(-1, 6115.17) * mm, "end": v(-37, 6183.17) * mm});
            skLineSegment(sketch, "E50.0.2.25", {"start": v(-37, 5697.17) * mm, "end": v(-37, 5975.17) * mm, "construction": true});
            skLineSegment(sketch, "E50.0.2.26", {"start": v(-1, 5281.17) * mm, "end": v(-37, 5349.17) * mm});
            skLineSegment(sketch, "E50.0.2.27", {"start": v(0, 5281.17) * mm, "end": v(-36, 5349.17) * mm});
            skLineSegment(sketch, "E50.0.2.28", {"start": v(0, 6043.17) * mm, "end": v(0, 6115.17) * mm});
            skLineSegment(sketch, "E50.0.2.29", {"start": v(-36, 5975.17) * mm, "end": v(0, 6043.17) * mm});
            skLineSegment(sketch, "E50.0.2.30", {"start": v(0, 5209.17) * mm, "end": v(0, 5281.17) * mm});
            skLineSegment(sketch, "E50.0.2.31", {"start": v(-1, 5209.17) * mm, "end": v(-1, 5281.17) * mm});
            skLineSegment(sketch, "E50.0.2.32", {"start": v(-37, 5975.17) * mm, "end": v(-1, 6043.17) * mm});
            skLineSegment(sketch, "E50.0.2.33", {"start": v(-1, 6043.17) * mm, "end": v(-1, 6115.17) * mm});
            skLineSegment(sketch, "E50.0.2.34", {"start": v(-37, 5627.17) * mm, "end": v(-37, 5697.17) * mm});
            skLineSegment(sketch, "E50.0.2.35", {"start": v(-1, 5487.17) * mm, "end": v(-1, 5559.17) * mm});
            skLineSegment(sketch, "E50.0.2.36", {"start": v(-37, 5071.17) * mm, "end": v(-37, 5141.17) * mm});
            skLineSegment(sketch, "E50.0.2.37", {"start": v(-1, 5837.17) * mm, "end": v(-37, 5905.17) * mm});
            skLineSegment(sketch, "E50.0.2.38", {"start": v(-36, 5419.17) * mm, "end": v(0, 5487.17) * mm});
            skLineSegment(sketch, "E50.0.2.39", {"start": v(-1, 5559.17) * mm, "end": v(-37, 5627.17) * mm});
            skLineSegment(sketch, "E50.0.2.40", {"start": v(0, 5765.17) * mm, "end": v(0, 5837.17) * mm});
            skLineSegment(sketch, "E50.0.2.41", {"start": v(-36, 5697.17) * mm, "end": v(0, 5765.17) * mm});
            skLineSegment(sketch, "E50.0.2.42", {"start": v(0, 5487.17) * mm, "end": v(0, 5559.17) * mm});
            skLineSegment(sketch, "E50.0.2.43", {"start": v(-36, 5071.17) * mm, "end": v(-36, 5141.17) * mm});
            skLineSegment(sketch, "E50.0.2.44", {"start": v(-37, 5419.17) * mm, "end": v(-1, 5487.17) * mm});
            skLineSegment(sketch, "E50.0.2.45", {"start": v(-37, 5141.17) * mm, "end": v(-1, 5209.17) * mm});
            skLineSegment(sketch, "E50.0.2.46", {"start": v(-1, 5003.17) * mm, "end": v(-37, 5071.17) * mm});
            skLineSegment(sketch, "E50.0.2.47", {"start": v(-1, 5765.17) * mm, "end": v(-1, 5837.17) * mm});
            skLineSegment(sketch, "E50.0.2.48", {"start": v(-37, 5349.17) * mm, "end": v(-37, 5419.17) * mm});
            skLineSegment(sketch, "E50.0.2.49", {"start": v(-37, 5905.17) * mm, "end": v(-37, 5975.17) * mm});
            skLineSegment(sketch, "E50.0.2.50", {"start": v(-36, 5349.17) * mm, "end": v(-36, 5419.17) * mm});
            skLineSegment(sketch, "E50.0.2.51", {"start": v(0, 5003.17) * mm, "end": v(-36, 5071.17) * mm});
            skLineSegment(sketch, "E50.0.2.52", {"start": v(-36, 5141.17) * mm, "end": v(0, 5209.17) * mm});
            skLineSegment(sketch, "E50.0.2.53", {"start": v(-36, 5905.17) * mm, "end": v(-36, 5975.17) * mm});
            skLineSegment(sketch, "E50.0.2.54", {"start": v(-36, 5627.17) * mm, "end": v(-36, 5697.17) * mm});
            skLineSegment(sketch, "E50.0.2.55", {"start": v(0, 5837.17) * mm, "end": v(-36, 5905.17) * mm});
            skLineSegment(sketch, "E50.0.2.56", {"start": v(0, 5559.17) * mm, "end": v(-36, 5627.17) * mm});
            skLineSegment(sketch, "E50.0.2.57", {"start": v(-37, 5697.17) * mm, "end": v(-1, 5765.17) * mm});
            skLineSegment(sketch, "E50.0.3.0", {"start": v(0, 6671.17) * mm, "end": v(-36, 6739.17) * mm});
            skLineSegment(sketch, "E50.0.3.1", {"start": v(-1, 6671.17) * mm, "end": v(-37, 6739.17) * mm});
            skLineSegment(sketch, "E50.0.3.2", {"start": v(0, 6599.17) * mm, "end": v(0, 6671.17) * mm});
            skLineSegment(sketch, "E50.0.3.3", {"start": v(0, 6321.17) * mm, "end": v(0, 6393.17) * mm});
            skLineSegment(sketch, "E50.0.3.4", {"start": v(-37, 6531.17) * mm, "end": v(-1, 6599.17) * mm});
            skLineSegment(sketch, "E50.0.3.5", {"start": v(-37, 6461.17) * mm, "end": v(-37, 6531.17) * mm});
            skLineSegment(sketch, "E50.0.3.6", {"start": v(-37, 6809.17) * mm, "end": v(-1, 6877.17) * mm});
            skLineSegment(sketch, "E50.0.3.7", {"start": v(-1, 6393.17) * mm, "end": v(-37, 6461.17) * mm});
            skLineSegment(sketch, "E50.0.3.8", {"start": v(-36, 6809.17) * mm, "end": v(0, 6877.17) * mm});
            skLineSegment(sketch, "E50.0.3.9", {"start": v(-36, 6461.17) * mm, "end": v(-36, 6531.17) * mm});
            skLineSegment(sketch, "E50.0.3.10", {"start": v(-37, 6183.17) * mm, "end": v(-37, 6253.17) * mm});
            skLineSegment(sketch, "E50.0.3.11", {"start": v(-36, 6739.17) * mm, "end": v(-36, 6809.17) * mm});
            skLineSegment(sketch, "E50.0.3.12", {"start": v(-1, 6599.17) * mm, "end": v(-1, 6671.17) * mm});
            skLineSegment(sketch, "E50.0.3.13", {"start": v(-37, 6253.17) * mm, "end": v(-1, 6321.17) * mm});
            skLineSegment(sketch, "E50.0.3.14", {"start": v(-36, 6253.17) * mm, "end": v(0, 6321.17) * mm});
            skLineSegment(sketch, "E50.0.3.15", {"start": v(0, 6877.17) * mm, "end": v(0, 6949.17) * mm});
            skLineSegment(sketch, "E50.0.3.16", {"start": v(0, 6393.17) * mm, "end": v(-36, 6461.17) * mm});
            skLineSegment(sketch, "E50.0.3.17", {"start": v(-36, 6183.17) * mm, "end": v(-36, 6253.17) * mm});
            skLineSegment(sketch, "E50.0.3.18", {"start": v(-1, 6321.17) * mm, "end": v(-1, 6393.17) * mm});
            skLineSegment(sketch, "E50.0.3.19", {"start": v(-36, 6531.17) * mm, "end": v(0, 6599.17) * mm});
            skLineSegment(sketch, "E50.0.3.20", {"start": v(-1, 6877.17) * mm, "end": v(-1, 6949.17) * mm});
            skLineSegment(sketch, "E50.0.3.21", {"start": v(-37, 6739.17) * mm, "end": v(-37, 6809.17) * mm});
            skLineSegment(sketch, "E50.0.3.22", {"start": v(-36, 7643.17) * mm, "end": v(-36, 7921.17) * mm, "construction": true});
            skLineSegment(sketch, "E50.0.3.23", {"start": v(0, 8061.17) * mm, "end": v(-36, 8129.17) * mm});
            skLineSegment(sketch, "E50.0.3.24", {"start": v(-1, 8061.17) * mm, "end": v(-37, 8129.17) * mm});
            skLineSegment(sketch, "E50.0.3.25", {"start": v(-37, 7643.17) * mm, "end": v(-37, 7921.17) * mm, "construction": true});
            skLineSegment(sketch, "E50.0.3.26", {"start": v(-1, 7227.17) * mm, "end": v(-37, 7295.17) * mm});
            skLineSegment(sketch, "E50.0.3.27", {"start": v(0, 7227.17) * mm, "end": v(-36, 7295.17) * mm});
            skLineSegment(sketch, "E50.0.3.28", {"start": v(0, 7989.17) * mm, "end": v(0, 8061.17) * mm});
            skLineSegment(sketch, "E50.0.3.29", {"start": v(-36, 7921.17) * mm, "end": v(0, 7989.17) * mm});
            skLineSegment(sketch, "E50.0.3.30", {"start": v(0, 7155.17) * mm, "end": v(0, 7227.17) * mm});
            skLineSegment(sketch, "E50.0.3.31", {"start": v(-1, 7155.17) * mm, "end": v(-1, 7227.17) * mm});
            skLineSegment(sketch, "E50.0.3.32", {"start": v(-37, 7921.17) * mm, "end": v(-1, 7989.17) * mm});
            skLineSegment(sketch, "E50.0.3.33", {"start": v(-1, 7989.17) * mm, "end": v(-1, 8061.17) * mm});
            skLineSegment(sketch, "E50.0.3.34", {"start": v(-37, 7573.17) * mm, "end": v(-37, 7643.17) * mm});
            skLineSegment(sketch, "E50.0.3.35", {"start": v(-1, 7433.17) * mm, "end": v(-1, 7505.17) * mm});
            skLineSegment(sketch, "E50.0.3.36", {"start": v(-37, 7017.17) * mm, "end": v(-37, 7087.17) * mm});
            skLineSegment(sketch, "E50.0.3.37", {"start": v(-1, 7783.17) * mm, "end": v(-37, 7851.17) * mm});
            skLineSegment(sketch, "E50.0.3.38", {"start": v(-36, 7365.17) * mm, "end": v(0, 7433.17) * mm});
            skLineSegment(sketch, "E50.0.3.39", {"start": v(-1, 7505.17) * mm, "end": v(-37, 7573.17) * mm});
            skLineSegment(sketch, "E50.0.3.40", {"start": v(0, 7711.17) * mm, "end": v(0, 7783.17) * mm});
            skLineSegment(sketch, "E50.0.3.41", {"start": v(-36, 7643.17) * mm, "end": v(0, 7711.17) * mm});
            skLineSegment(sketch, "E50.0.3.42", {"start": v(0, 7433.17) * mm, "end": v(0, 7505.17) * mm});
            skLineSegment(sketch, "E50.0.3.43", {"start": v(-36, 7017.17) * mm, "end": v(-36, 7087.17) * mm});
            skLineSegment(sketch, "E50.0.3.44", {"start": v(-37, 7365.17) * mm, "end": v(-1, 7433.17) * mm});
            skLineSegment(sketch, "E50.0.3.45", {"start": v(-37, 7087.17) * mm, "end": v(-1, 7155.17) * mm});
            skLineSegment(sketch, "E50.0.3.46", {"start": v(-1, 6949.17) * mm, "end": v(-37, 7017.17) * mm});
            skLineSegment(sketch, "E50.0.3.47", {"start": v(-1, 7711.17) * mm, "end": v(-1, 7783.17) * mm});
            skLineSegment(sketch, "E50.0.3.48", {"start": v(-37, 7295.17) * mm, "end": v(-37, 7365.17) * mm});
            skLineSegment(sketch, "E50.0.3.49", {"start": v(-37, 7851.17) * mm, "end": v(-37, 7921.17) * mm});
            skLineSegment(sketch, "E50.0.3.50", {"start": v(-36, 7295.17) * mm, "end": v(-36, 7365.17) * mm});
            skLineSegment(sketch, "E50.0.3.51", {"start": v(0, 6949.17) * mm, "end": v(-36, 7017.17) * mm});
            skLineSegment(sketch, "E50.0.3.52", {"start": v(-36, 7087.17) * mm, "end": v(0, 7155.17) * mm});
            skLineSegment(sketch, "E50.0.3.53", {"start": v(-36, 7851.17) * mm, "end": v(-36, 7921.17) * mm});
            skLineSegment(sketch, "E50.0.3.54", {"start": v(-36, 7573.17) * mm, "end": v(-36, 7643.17) * mm});
            skLineSegment(sketch, "E50.0.3.55", {"start": v(0, 7783.17) * mm, "end": v(-36, 7851.17) * mm});
            skLineSegment(sketch, "E50.0.3.56", {"start": v(0, 7505.17) * mm, "end": v(-36, 7573.17) * mm});
            skLineSegment(sketch, "E50.0.3.57", {"start": v(-37, 7643.17) * mm, "end": v(-1, 7711.17) * mm});
            skLineSegment(sketch, "E50.0.4.0", {"start": v(0, 8617.17) * mm, "end": v(-36, 8685.17) * mm});
            skLineSegment(sketch, "E50.0.4.1", {"start": v(-1, 8617.17) * mm, "end": v(-37, 8685.17) * mm});
            skLineSegment(sketch, "E50.0.4.2", {"start": v(0, 8545.17) * mm, "end": v(0, 8617.17) * mm});
            skLineSegment(sketch, "E50.0.4.3", {"start": v(0, 8267.17) * mm, "end": v(0, 8339.17) * mm});
            skLineSegment(sketch, "E50.0.4.4", {"start": v(-37, 8477.17) * mm, "end": v(-1, 8545.17) * mm});
            skLineSegment(sketch, "E50.0.4.5", {"start": v(-37, 8407.17) * mm, "end": v(-37, 8477.17) * mm});
            skLineSegment(sketch, "E50.0.4.6", {"start": v(-37, 8755.17) * mm, "end": v(-1, 8823.17) * mm});
            skLineSegment(sketch, "E50.0.4.7", {"start": v(-1, 8339.17) * mm, "end": v(-37, 8407.17) * mm});
            skLineSegment(sketch, "E50.0.4.8", {"start": v(-36, 8755.17) * mm, "end": v(0, 8823.17) * mm});
            skLineSegment(sketch, "E50.0.4.9", {"start": v(-36, 8407.17) * mm, "end": v(-36, 8477.17) * mm});
            skLineSegment(sketch, "E50.0.4.10", {"start": v(-37, 8129.17) * mm, "end": v(-37, 8199.17) * mm});
            skLineSegment(sketch, "E50.0.4.11", {"start": v(-36, 8685.17) * mm, "end": v(-36, 8755.17) * mm});
            skLineSegment(sketch, "E50.0.4.12", {"start": v(-1, 8545.17) * mm, "end": v(-1, 8617.17) * mm});
            skLineSegment(sketch, "E50.0.4.13", {"start": v(-37, 8199.17) * mm, "end": v(-1, 8267.17) * mm});
            skLineSegment(sketch, "E50.0.4.14", {"start": v(-36, 8199.17) * mm, "end": v(0, 8267.17) * mm});
            skLineSegment(sketch, "E50.0.4.15", {"start": v(0, 8823.17) * mm, "end": v(0, 8895.17) * mm});
            skLineSegment(sketch, "E50.0.4.16", {"start": v(0, 8339.17) * mm, "end": v(-36, 8407.17) * mm});
            skLineSegment(sketch, "E50.0.4.17", {"start": v(-36, 8129.17) * mm, "end": v(-36, 8199.17) * mm});
            skLineSegment(sketch, "E50.0.4.18", {"start": v(-1, 8267.17) * mm, "end": v(-1, 8339.17) * mm});
            skLineSegment(sketch, "E50.0.4.19", {"start": v(-36, 8477.17) * mm, "end": v(0, 8545.17) * mm});
            skLineSegment(sketch, "E50.0.4.20", {"start": v(-1, 8823.17) * mm, "end": v(-1, 8895.17) * mm});
            skLineSegment(sketch, "E50.0.4.21", {"start": v(-37, 8685.17) * mm, "end": v(-37, 8755.17) * mm});
            skLineSegment(sketch, "E50.0.4.22", {"start": v(-36, 9589.17) * mm, "end": v(-36, 9867.17) * mm, "construction": true});
            skLineSegment(sketch, "E50.0.4.23", {"start": v(0, 10007.17) * mm, "end": v(-36, 10075.17) * mm});
            skLineSegment(sketch, "E50.0.4.24", {"start": v(-1, 10007.17) * mm, "end": v(-37, 10075.17) * mm});
            skLineSegment(sketch, "E50.0.4.25", {"start": v(-37, 9589.17) * mm, "end": v(-37, 9867.17) * mm, "construction": true});
            skLineSegment(sketch, "E50.0.4.26", {"start": v(-1, 9173.17) * mm, "end": v(-37, 9241.17) * mm});
            skLineSegment(sketch, "E50.0.4.27", {"start": v(0, 9173.17) * mm, "end": v(-36, 9241.17) * mm});
            skLineSegment(sketch, "E50.0.4.28", {"start": v(0, 9935.17) * mm, "end": v(0, 10007.17) * mm});
            skLineSegment(sketch, "E50.0.4.29", {"start": v(-36, 9867.17) * mm, "end": v(0, 9935.17) * mm});
            skLineSegment(sketch, "E50.0.4.30", {"start": v(0, 9101.17) * mm, "end": v(0, 9173.17) * mm});
            skLineSegment(sketch, "E50.0.4.31", {"start": v(-1, 9101.17) * mm, "end": v(-1, 9173.17) * mm});
            skLineSegment(sketch, "E50.0.4.32", {"start": v(-37, 9867.17) * mm, "end": v(-1, 9935.17) * mm});
            skLineSegment(sketch, "E50.0.4.33", {"start": v(-1, 9935.17) * mm, "end": v(-1, 10007.17) * mm});
            skLineSegment(sketch, "E50.0.4.34", {"start": v(-37, 9519.17) * mm, "end": v(-37, 9589.17) * mm});
            skLineSegment(sketch, "E50.0.4.35", {"start": v(-1, 9379.17) * mm, "end": v(-1, 9451.17) * mm});
            skLineSegment(sketch, "E50.0.4.36", {"start": v(-37, 8963.17) * mm, "end": v(-37, 9033.17) * mm});
            skLineSegment(sketch, "E50.0.4.37", {"start": v(-1, 9729.17) * mm, "end": v(-37, 9797.17) * mm});
            skLineSegment(sketch, "E50.0.4.38", {"start": v(-36, 9311.17) * mm, "end": v(0, 9379.17) * mm});
            skLineSegment(sketch, "E50.0.4.39", {"start": v(-1, 9451.17) * mm, "end": v(-37, 9519.17) * mm});
            skLineSegment(sketch, "E50.0.4.40", {"start": v(0, 9657.17) * mm, "end": v(0, 9729.17) * mm});
            skLineSegment(sketch, "E50.0.4.41", {"start": v(-36, 9589.17) * mm, "end": v(0, 9657.17) * mm});
            skLineSegment(sketch, "E50.0.4.42", {"start": v(0, 9379.17) * mm, "end": v(0, 9451.17) * mm});
            skLineSegment(sketch, "E50.0.4.43", {"start": v(-36, 8963.17) * mm, "end": v(-36, 9033.17) * mm});
            skLineSegment(sketch, "E50.0.4.44", {"start": v(-37, 9311.17) * mm, "end": v(-1, 9379.17) * mm});
            skLineSegment(sketch, "E50.0.4.45", {"start": v(-37, 9033.17) * mm, "end": v(-1, 9101.17) * mm});
            skLineSegment(sketch, "E50.0.4.46", {"start": v(-1, 8895.17) * mm, "end": v(-37, 8963.17) * mm});
            skLineSegment(sketch, "E50.0.4.47", {"start": v(-1, 9657.17) * mm, "end": v(-1, 9729.17) * mm});
            skLineSegment(sketch, "E50.0.4.48", {"start": v(-37, 9241.17) * mm, "end": v(-37, 9311.17) * mm});
            skLineSegment(sketch, "E50.0.4.49", {"start": v(-37, 9797.17) * mm, "end": v(-37, 9867.17) * mm});
            skLineSegment(sketch, "E50.0.4.50", {"start": v(-36, 9241.17) * mm, "end": v(-36, 9311.17) * mm});
            skLineSegment(sketch, "E50.0.4.51", {"start": v(0, 8895.17) * mm, "end": v(-36, 8963.17) * mm});
            skLineSegment(sketch, "E50.0.4.52", {"start": v(-36, 9033.17) * mm, "end": v(0, 9101.17) * mm});
            skLineSegment(sketch, "E50.0.4.53", {"start": v(-36, 9797.17) * mm, "end": v(-36, 9867.17) * mm});
            skLineSegment(sketch, "E50.0.4.54", {"start": v(-36, 9519.17) * mm, "end": v(-36, 9589.17) * mm});
            skLineSegment(sketch, "E50.0.4.55", {"start": v(0, 9729.17) * mm, "end": v(-36, 9797.17) * mm});
            skLineSegment(sketch, "E50.0.4.56", {"start": v(0, 9451.17) * mm, "end": v(-36, 9519.17) * mm});
            skLineSegment(sketch, "E50.0.4.57", {"start": v(-37, 9589.17) * mm, "end": v(-1, 9657.17) * mm});
            skLineSegment(sketch, "E50.0.5.0", {"start": v(0, 10563.17) * mm, "end": v(-36, 10631.17) * mm});
            skLineSegment(sketch, "E50.0.5.1", {"start": v(-1, 10563.17) * mm, "end": v(-37, 10631.17) * mm});
            skLineSegment(sketch, "E50.0.5.2", {"start": v(0, 10491.17) * mm, "end": v(0, 10563.17) * mm});
            skLineSegment(sketch, "E50.0.5.3", {"start": v(0, 10213.17) * mm, "end": v(0, 10285.17) * mm});
            skLineSegment(sketch, "E50.0.5.4", {"start": v(-37, 10423.17) * mm, "end": v(-1, 10491.17) * mm});
            skLineSegment(sketch, "E50.0.5.5", {"start": v(-37, 10353.17) * mm, "end": v(-37, 10423.17) * mm});
            skLineSegment(sketch, "E50.0.5.6", {"start": v(-37, 10701.17) * mm, "end": v(-1, 10769.17) * mm});
            skLineSegment(sketch, "E50.0.5.7", {"start": v(-1, 10285.17) * mm, "end": v(-37, 10353.17) * mm});
            skLineSegment(sketch, "E50.0.5.8", {"start": v(-36, 10701.17) * mm, "end": v(0, 10769.17) * mm});
            skLineSegment(sketch, "E50.0.5.9", {"start": v(-36, 10353.17) * mm, "end": v(-36, 10423.17) * mm});
            skLineSegment(sketch, "E50.0.5.10", {"start": v(-37, 10075.17) * mm, "end": v(-37, 10145.17) * mm});
            skLineSegment(sketch, "E50.0.5.11", {"start": v(-36, 10631.17) * mm, "end": v(-36, 10701.17) * mm});
            skLineSegment(sketch, "E50.0.5.12", {"start": v(-1, 10491.17) * mm, "end": v(-1, 10563.17) * mm});
            skLineSegment(sketch, "E50.0.5.13", {"start": v(-37, 10145.17) * mm, "end": v(-1, 10213.17) * mm});
            skLineSegment(sketch, "E50.0.5.14", {"start": v(-36, 10145.17) * mm, "end": v(0, 10213.17) * mm});
            skLineSegment(sketch, "E50.0.5.15", {"start": v(0, 10769.17) * mm, "end": v(0, 10841.17) * mm});
            skLineSegment(sketch, "E50.0.5.16", {"start": v(0, 10285.17) * mm, "end": v(-36, 10353.17) * mm});
            skLineSegment(sketch, "E50.0.5.17", {"start": v(-36, 10075.17) * mm, "end": v(-36, 10145.17) * mm});
            skLineSegment(sketch, "E50.0.5.18", {"start": v(-1, 10213.17) * mm, "end": v(-1, 10285.17) * mm});
            skLineSegment(sketch, "E50.0.5.19", {"start": v(-36, 10423.17) * mm, "end": v(0, 10491.17) * mm});
            skLineSegment(sketch, "E50.0.5.20", {"start": v(-1, 10769.17) * mm, "end": v(-1, 10841.17) * mm});
            skLineSegment(sketch, "E50.0.5.21", {"start": v(-37, 10631.17) * mm, "end": v(-37, 10701.17) * mm});
            skLineSegment(sketch, "E50.0.5.22", {"start": v(-36, 11535.17) * mm, "end": v(-36, 11813.17) * mm, "construction": true});
            skLineSegment(sketch, "E50.0.5.23", {"start": v(0, 11953.17) * mm, "end": v(-36, 12021.17) * mm});
            skLineSegment(sketch, "E50.0.5.24", {"start": v(-1, 11953.17) * mm, "end": v(-37, 12021.17) * mm});
            skLineSegment(sketch, "E50.0.5.25", {"start": v(-37, 11535.17) * mm, "end": v(-37, 11813.17) * mm, "construction": true});
            skLineSegment(sketch, "E50.0.5.26", {"start": v(-1, 11119.17) * mm, "end": v(-37, 11187.17) * mm});
            skLineSegment(sketch, "E50.0.5.27", {"start": v(0, 11119.17) * mm, "end": v(-36, 11187.17) * mm});
            skLineSegment(sketch, "E50.0.5.28", {"start": v(0, 11881.17) * mm, "end": v(0, 11953.17) * mm});
            skLineSegment(sketch, "E50.0.5.29", {"start": v(-36, 11813.17) * mm, "end": v(0, 11881.17) * mm});
            skLineSegment(sketch, "E50.0.5.30", {"start": v(0, 11047.17) * mm, "end": v(0, 11119.17) * mm});
            skLineSegment(sketch, "E50.0.5.31", {"start": v(-1, 11047.17) * mm, "end": v(-1, 11119.17) * mm});
            skLineSegment(sketch, "E50.0.5.32", {"start": v(-37, 11813.17) * mm, "end": v(-1, 11881.17) * mm});
            skLineSegment(sketch, "E50.0.5.33", {"start": v(-1, 11881.17) * mm, "end": v(-1, 11953.17) * mm});
            skLineSegment(sketch, "E50.0.5.34", {"start": v(-37, 11465.17) * mm, "end": v(-37, 11535.17) * mm});
            skLineSegment(sketch, "E50.0.5.35", {"start": v(-1, 11325.17) * mm, "end": v(-1, 11397.17) * mm});
            skLineSegment(sketch, "E50.0.5.36", {"start": v(-37, 10909.17) * mm, "end": v(-37, 10979.17) * mm});
            skLineSegment(sketch, "E50.0.5.37", {"start": v(-1, 11675.17) * mm, "end": v(-37, 11743.17) * mm});
            skLineSegment(sketch, "E50.0.5.38", {"start": v(-36, 11257.17) * mm, "end": v(0, 11325.17) * mm});
            skLineSegment(sketch, "E50.0.5.39", {"start": v(-1, 11397.17) * mm, "end": v(-37, 11465.17) * mm});
            skLineSegment(sketch, "E50.0.5.40", {"start": v(0, 11603.17) * mm, "end": v(0, 11675.17) * mm});
            skLineSegment(sketch, "E50.0.5.41", {"start": v(-36, 11535.17) * mm, "end": v(0, 11603.17) * mm});
            skLineSegment(sketch, "E50.0.5.42", {"start": v(0, 11325.17) * mm, "end": v(0, 11397.17) * mm});
            skLineSegment(sketch, "E50.0.5.43", {"start": v(-36, 10909.17) * mm, "end": v(-36, 10979.17) * mm});
            skLineSegment(sketch, "E50.0.5.44", {"start": v(-37, 11257.17) * mm, "end": v(-1, 11325.17) * mm});
            skLineSegment(sketch, "E50.0.5.45", {"start": v(-37, 10979.17) * mm, "end": v(-1, 11047.17) * mm});
            skLineSegment(sketch, "E50.0.5.46", {"start": v(-1, 10841.17) * mm, "end": v(-37, 10909.17) * mm});
            skLineSegment(sketch, "E50.0.5.47", {"start": v(-1, 11603.17) * mm, "end": v(-1, 11675.17) * mm});
            skLineSegment(sketch, "E50.0.5.48", {"start": v(-37, 11187.17) * mm, "end": v(-37, 11257.17) * mm});
            skLineSegment(sketch, "E50.0.5.49", {"start": v(-37, 11743.17) * mm, "end": v(-37, 11813.17) * mm});
            skLineSegment(sketch, "E50.0.5.50", {"start": v(-36, 11187.17) * mm, "end": v(-36, 11257.17) * mm});
            skLineSegment(sketch, "E50.0.5.51", {"start": v(0, 10841.17) * mm, "end": v(-36, 10909.17) * mm});
            skLineSegment(sketch, "E50.0.5.52", {"start": v(-36, 10979.17) * mm, "end": v(0, 11047.17) * mm});
            skLineSegment(sketch, "E50.0.5.53", {"start": v(-36, 11743.17) * mm, "end": v(-36, 11813.17) * mm});
            skLineSegment(sketch, "E50.0.5.54", {"start": v(-36, 11465.17) * mm, "end": v(-36, 11535.17) * mm});
            skLineSegment(sketch, "E50.0.5.55", {"start": v(0, 11675.17) * mm, "end": v(-36, 11743.17) * mm});
            skLineSegment(sketch, "E50.0.5.56", {"start": v(0, 11397.17) * mm, "end": v(-36, 11465.17) * mm});
            skLineSegment(sketch, "E50.0.5.57", {"start": v(-37, 11535.17) * mm, "end": v(-1, 11603.17) * mm});
            skLineSegment(sketch, "E50.direction1", {"start": v(-37, 345.17) * mm, "end": v(-12, 345.17) * mm, "construction": true});
            skLineSegment(sketch, "E50.direction2", {"start": v(-37, 345.17) * mm, "end": v(-37, 2291.17) * mm, "construction": true});
            skLineSegment(sketch, "E51", {"start": v(-36, 12021.17) * mm, "end": v(-36, 12092) * mm});
            skLineSegment(sketch, "E52", {"start": v(-36, 12092) * mm, "end": v(-37, 12092) * mm});
            skLineSegment(sketch, "E53", {"start": v(-37, 12092) * mm, "end": v(-37, 12021.17) * mm});
            skSolve(sketch);
        }
        {
            var Q0;
            Q0 = qSketchRegion(id + "F12", true);
            extrude(context, id + "F13", {"entities" : qUnion([Q0]), "operationType" : NewBodyOperationType.ADD, "depth" : 2696 * mm, "offsetDistance" : 25 * mm});
        }
        {
            var Q0;
            {var subQ20=makeQuery(id+"F1.opExtrude","SWEPT_FACE",FACE,{"disambiguationData":[OSD([sQuery(id+"F0.wireOp",EDGE,"E0.right")])]});var subQ21=makeQuery(id+"F3.boolean.opBoolean","COPY",FACE,{"derivedFrom":makeQuery(id+"F3.opExtrude","SWEPT_FACE",FACE,{"disambiguationData":[OSD([sQuery(id+"F2.wireOp",EDGE,"E3")])]})});var subQ22=makeQuery(id+"F5.opExtrude","SWEPT_FACE",FACE,{"disambiguationData":[OSD([sQuery(id+"F4.wireOp",EDGE,"E8")])]});var subQ29=makeQuery(id+"F1.opExtrude","SWEPT_FACE",FACE,{"disambiguationData":[OSD([sQuery(id+"F0.wireOp",EDGE,"E0.left")])]});Q0=makeQuery(id+"F13.boolean.opBoolean","SPLIT",FACE,{"disambiguationData":[TD([subQ20])],"derivedFrom":makeQuery(id+"F11.boolean.opBoolean","SPLIT",FACE,{"disambiguationData":[TD([subQ29])],"derivedFrom":makeQuery(id+"F9.boolean.opBoolean","SPLIT",FACE,{"disambiguationData":[TD([makeQuery(id+"F1.opExtrude","SWEPT_FACE",FACE,{"disambiguationData":[OSD([sQuery(id+"F0.wireOp",EDGE,"E0.top")])]})])],"derivedFrom":makeQuery(id+"F5.boolean.opBoolean","MERGE",FACE,{"derivedFrom":[subQ21],"fromTools":[subQ22]})})})});}
            var sketch = newSketch(context, id + "F14", { "sketchPlane" : qUnion([Q0])});
            skLineSegment(sketch, "E54", {"start": v(-2402, 12091.83) * mm, "end": v(-2402, 12054.83) * mm});
            skLineSegment(sketch, "E55", {"start": v(-2438, 11986.83) * mm, "end": v(-2438, 11914.83) * mm});
            skLineSegment(sketch, "E56", {"start": v(-2402, 11846.83) * mm, "end": v(-2402, 11776.83) * mm});
            skLineSegment(sketch, "E57", {"start": v(-2402, 12054.83) * mm, "end": v(-2438, 11986.83) * mm});
            skLineSegment(sketch, "E58", {"start": v(-2438, 11914.83) * mm, "end": v(-2402, 11846.83) * mm});
            skLineSegment(sketch, "E59.1.0.0", {"start": v(-2402, 11776.83) * mm, "end": v(-2438, 11708.83) * mm});
            skLineSegment(sketch, "E59.1.0.1", {"start": v(-2438, 11708.83) * mm, "end": v(-2438, 11636.83) * mm});
            skLineSegment(sketch, "E59.1.0.2", {"start": v(-2438, 11636.83) * mm, "end": v(-2402, 11568.83) * mm});
            skLineSegment(sketch, "E59.1.0.3", {"start": v(-2402, 11568.83) * mm, "end": v(-2402, 11498.83) * mm});
            skLineSegment(sketch, "E59.2.0.0", {"start": v(-2402, 11498.83) * mm, "end": v(-2438, 11430.83) * mm});
            skLineSegment(sketch, "E59.2.0.1", {"start": v(-2438, 11430.83) * mm, "end": v(-2438, 11358.83) * mm});
            skLineSegment(sketch, "E59.2.0.2", {"start": v(-2438, 11358.83) * mm, "end": v(-2402, 11290.83) * mm});
            skLineSegment(sketch, "E59.2.0.3", {"start": v(-2402, 11290.83) * mm, "end": v(-2402, 11220.83) * mm});
            skLineSegment(sketch, "E59.3.0.0", {"start": v(-2402, 11220.83) * mm, "end": v(-2438, 11152.83) * mm});
            skLineSegment(sketch, "E59.3.0.1", {"start": v(-2438, 11152.83) * mm, "end": v(-2438, 11080.83) * mm});
            skLineSegment(sketch, "E59.3.0.2", {"start": v(-2438, 11080.83) * mm, "end": v(-2402, 11012.83) * mm});
            skLineSegment(sketch, "E59.3.0.3", {"start": v(-2402, 11012.83) * mm, "end": v(-2402, 10942.83) * mm});
            skLineSegment(sketch, "E59.4.0.0", {"start": v(-2402, 10942.83) * mm, "end": v(-2438, 10874.83) * mm});
            skLineSegment(sketch, "E59.4.0.1", {"start": v(-2438, 10874.83) * mm, "end": v(-2438, 10802.83) * mm});
            skLineSegment(sketch, "E59.4.0.2", {"start": v(-2438, 10802.83) * mm, "end": v(-2402, 10734.83) * mm});
            skLineSegment(sketch, "E59.4.0.3", {"start": v(-2402, 10734.83) * mm, "end": v(-2402, 10664.83) * mm});
            skLineSegment(sketch, "E59.5.0.0", {"start": v(-2402, 10664.83) * mm, "end": v(-2438, 10596.83) * mm});
            skLineSegment(sketch, "E59.5.0.1", {"start": v(-2438, 10596.83) * mm, "end": v(-2438, 10524.83) * mm});
            skLineSegment(sketch, "E59.5.0.2", {"start": v(-2438, 10524.83) * mm, "end": v(-2402, 10456.83) * mm});
            skLineSegment(sketch, "E59.5.0.3", {"start": v(-2402, 10456.83) * mm, "end": v(-2402, 10386.83) * mm});
            skLineSegment(sketch, "E59.6.0.0", {"start": v(-2402, 10386.83) * mm, "end": v(-2438, 10318.83) * mm});
            skLineSegment(sketch, "E59.6.0.1", {"start": v(-2438, 10318.83) * mm, "end": v(-2438, 10246.83) * mm});
            skLineSegment(sketch, "E59.6.0.2", {"start": v(-2438, 10246.83) * mm, "end": v(-2402, 10178.83) * mm});
            skLineSegment(sketch, "E59.6.0.3", {"start": v(-2402, 10178.83) * mm, "end": v(-2402, 10108.83) * mm});
            skLineSegment(sketch, "E59.direction1", {"start": v(-2402, 12054.83) * mm, "end": v(-2402, 11776.83) * mm, "construction": true});
            skLineSegment(sketch, "E60.1.0.0", {"start": v(-2402, 10108.83) * mm, "end": v(-2438, 10040.83) * mm});
            skLineSegment(sketch, "E60.1.0.1", {"start": v(-2438, 10040.83) * mm, "end": v(-2438, 9968.83) * mm});
            skLineSegment(sketch, "E60.1.0.2", {"start": v(-2438, 9968.83) * mm, "end": v(-2402, 9900.83) * mm});
            skLineSegment(sketch, "E60.direction1", {"start": v(-2402, 10386.83) * mm, "end": v(-2402, 10108.83) * mm, "construction": true});
            skLineSegment(sketch, "E61.0.1.0", {"start": v(-2401, 12054.83) * mm, "end": v(-2401, 11776.83) * mm, "construction": true});
            skLineSegment(sketch, "E61.0.1.1", {"start": v(-2401, 10386.83) * mm, "end": v(-2401, 10108.83) * mm, "construction": true});
            skLineSegment(sketch, "E61.0.1.2", {"start": v(-2401, 10108.83) * mm, "end": v(-2437, 10040.83) * mm});
            skLineSegment(sketch, "E61.0.1.3", {"start": v(-2401, 11012.83) * mm, "end": v(-2401, 10942.83) * mm});
            skLineSegment(sketch, "E61.0.1.5", {"start": v(-2437, 11358.83) * mm, "end": v(-2401, 11290.83) * mm});
            skLineSegment(sketch, "E61.0.1.6", {"start": v(-2401, 11220.83) * mm, "end": v(-2437, 11152.83) * mm});
            skLineSegment(sketch, "E61.0.1.7", {"start": v(-2437, 10802.83) * mm, "end": v(-2401, 10734.83) * mm});
            skLineSegment(sketch, "E61.0.1.8", {"start": v(-2401, 10386.83) * mm, "end": v(-2437, 10318.83) * mm});
            skLineSegment(sketch, "E61.0.1.9", {"start": v(-2437, 11708.83) * mm, "end": v(-2437, 11636.83) * mm});
            skLineSegment(sketch, "E61.0.1.10", {"start": v(-2437, 9968.83) * mm, "end": v(-2401, 9900.83) * mm});
            skLineSegment(sketch, "E61.0.1.11", {"start": v(-2401, 10664.83) * mm, "end": v(-2437, 10596.83) * mm});
            skLineSegment(sketch, "E61.0.1.12", {"start": v(-2437, 11636.83) * mm, "end": v(-2401, 11568.83) * mm});
            skLineSegment(sketch, "E61.0.1.13", {"start": v(-2401, 11776.83) * mm, "end": v(-2437, 11708.83) * mm});
            skLineSegment(sketch, "E61.0.1.14", {"start": v(-2437, 10246.83) * mm, "end": v(-2401, 10178.83) * mm});
            skLineSegment(sketch, "E61.0.1.15", {"start": v(-2437, 11430.83) * mm, "end": v(-2437, 11358.83) * mm});
            skLineSegment(sketch, "E61.0.1.16", {"start": v(-2401, 10942.83) * mm, "end": v(-2437, 10874.83) * mm});
            skLineSegment(sketch, "E61.0.1.17", {"start": v(-2401, 11498.83) * mm, "end": v(-2437, 11430.83) * mm});
            skLineSegment(sketch, "E61.0.1.18", {"start": v(-2437, 10040.83) * mm, "end": v(-2437, 9968.83) * mm});
            skLineSegment(sketch, "E61.0.1.19", {"start": v(-2401, 10734.83) * mm, "end": v(-2401, 10664.83) * mm});
            skLineSegment(sketch, "E61.0.1.20", {"start": v(-2437, 10596.83) * mm, "end": v(-2437, 10524.83) * mm});
            skLineSegment(sketch, "E61.0.1.21", {"start": v(-2437, 10524.83) * mm, "end": v(-2401, 10456.83) * mm});
            skLineSegment(sketch, "E61.0.1.22", {"start": v(-2401, 11568.83) * mm, "end": v(-2401, 11498.83) * mm});
            skLineSegment(sketch, "E61.0.1.23", {"start": v(-2437, 10318.83) * mm, "end": v(-2437, 10246.83) * mm});
            skLineSegment(sketch, "E61.0.1.24", {"start": v(-2437, 11914.83) * mm, "end": v(-2401, 11846.83) * mm});
            skLineSegment(sketch, "E61.0.1.25", {"start": v(-2437, 10874.83) * mm, "end": v(-2437, 10802.83) * mm});
            skLineSegment(sketch, "E61.0.1.26", {"start": v(-2401, 12054.83) * mm, "end": v(-2437, 11986.83) * mm});
            skLineSegment(sketch, "E61.0.1.27", {"start": v(-2401, 11290.83) * mm, "end": v(-2401, 11220.83) * mm});
            skLineSegment(sketch, "E61.0.1.28", {"start": v(-2437, 11152.83) * mm, "end": v(-2437, 11080.83) * mm});
            skLineSegment(sketch, "E61.0.1.29", {"start": v(-2437, 11986.83) * mm, "end": v(-2437, 11914.83) * mm});
            skLineSegment(sketch, "E61.0.1.30", {"start": v(-2437, 11080.83) * mm, "end": v(-2401, 11012.83) * mm});
            skLineSegment(sketch, "E61.0.1.31", {"start": v(-2401, 10178.83) * mm, "end": v(-2401, 10108.83) * mm});
            skLineSegment(sketch, "E61.0.1.32", {"start": v(-2401, 11846.83) * mm, "end": v(-2401, 11776.83) * mm});
            skLineSegment(sketch, "E61.0.1.33", {"start": v(-2401, 10456.83) * mm, "end": v(-2401, 10386.83) * mm});
            skLineSegment(sketch, "E61.0.1.34", {"start": v(-2401, 12091.83) * mm, "end": v(-2401, 12054.83) * mm});
            skLineSegment(sketch, "E62", {"start": v(-2401, 12091.83) * mm, "end": v(-2401, 12092) * mm});
            skLineSegment(sketch, "E63", {"start": v(-2401, 12092) * mm, "end": v(-2402, 12092) * mm});
            skLineSegment(sketch, "E64", {"start": v(-2402, 12092) * mm, "end": v(-2402, 12091.83) * mm});
            skLineSegment(sketch, "E65.0.1.0", {"start": v(-2438, 9412.83) * mm, "end": v(-2402, 9344.83) * mm});
            skLineSegment(sketch, "E65.0.1.1", {"start": v(-2437, 9412.83) * mm, "end": v(-2401, 9344.83) * mm});
            skLineSegment(sketch, "E65.0.1.2", {"start": v(-2438, 9484.83) * mm, "end": v(-2438, 9412.83) * mm});
            skLineSegment(sketch, "E65.0.1.3", {"start": v(-2438, 9762.83) * mm, "end": v(-2438, 9690.83) * mm});
            skLineSegment(sketch, "E65.0.1.4", {"start": v(-2401, 9552.83) * mm, "end": v(-2437, 9484.83) * mm});
            skLineSegment(sketch, "E65.0.1.5", {"start": v(-2401, 9622.83) * mm, "end": v(-2401, 9552.83) * mm});
            skLineSegment(sketch, "E65.0.1.6", {"start": v(-2401, 9274.83) * mm, "end": v(-2437, 9206.83) * mm});
            skLineSegment(sketch, "E65.0.1.7", {"start": v(-2437, 9690.83) * mm, "end": v(-2401, 9622.83) * mm});
            skLineSegment(sketch, "E65.0.1.8", {"start": v(-2402, 9274.83) * mm, "end": v(-2438, 9206.83) * mm});
            skLineSegment(sketch, "E65.0.1.9", {"start": v(-2402, 9622.83) * mm, "end": v(-2402, 9552.83) * mm});
            skLineSegment(sketch, "E65.0.1.10", {"start": v(-2401, 9900.83) * mm, "end": v(-2401, 9830.83) * mm});
            skLineSegment(sketch, "E65.0.1.11", {"start": v(-2402, 9344.83) * mm, "end": v(-2402, 9274.83) * mm});
            skLineSegment(sketch, "E65.0.1.12", {"start": v(-2437, 9484.83) * mm, "end": v(-2437, 9412.83) * mm});
            skLineSegment(sketch, "E65.0.1.13", {"start": v(-2401, 9830.83) * mm, "end": v(-2437, 9762.83) * mm});
            skLineSegment(sketch, "E65.0.1.14", {"start": v(-2402, 9830.83) * mm, "end": v(-2438, 9762.83) * mm});
            skLineSegment(sketch, "E65.0.1.15", {"start": v(-2438, 9206.83) * mm, "end": v(-2438, 9134.83) * mm});
            skLineSegment(sketch, "E65.0.1.16", {"start": v(-2438, 9690.83) * mm, "end": v(-2402, 9622.83) * mm});
            skLineSegment(sketch, "E65.0.1.17", {"start": v(-2402, 9900.83) * mm, "end": v(-2402, 9830.83) * mm});
            skLineSegment(sketch, "E65.0.1.18", {"start": v(-2437, 9762.83) * mm, "end": v(-2437, 9690.83) * mm});
            skLineSegment(sketch, "E65.0.1.19", {"start": v(-2402, 9552.83) * mm, "end": v(-2438, 9484.83) * mm});
            skLineSegment(sketch, "E65.0.1.20", {"start": v(-2437, 9206.83) * mm, "end": v(-2437, 9134.83) * mm});
            skLineSegment(sketch, "E65.0.1.21", {"start": v(-2401, 9344.83) * mm, "end": v(-2401, 9274.83) * mm});
            skLineSegment(sketch, "E65.0.1.22", {"start": v(-2402, 8440.83) * mm, "end": v(-2402, 8162.83) * mm, "construction": true});
            skLineSegment(sketch, "E65.0.1.23", {"start": v(-2438, 8022.83) * mm, "end": v(-2402, 7954.83) * mm});
            skLineSegment(sketch, "E65.0.1.24", {"start": v(-2437, 8022.83) * mm, "end": v(-2401, 7954.83) * mm});
            skLineSegment(sketch, "E65.0.1.25", {"start": v(-2401, 8440.83) * mm, "end": v(-2401, 8162.83) * mm, "construction": true});
            skLineSegment(sketch, "E65.0.1.26", {"start": v(-2437, 8856.83) * mm, "end": v(-2401, 8788.83) * mm});
            skLineSegment(sketch, "E65.0.1.27", {"start": v(-2438, 8856.83) * mm, "end": v(-2402, 8788.83) * mm});
            skLineSegment(sketch, "E65.0.1.28", {"start": v(-2438, 8094.83) * mm, "end": v(-2438, 8022.83) * mm});
            skLineSegment(sketch, "E65.0.1.29", {"start": v(-2402, 8162.83) * mm, "end": v(-2438, 8094.83) * mm});
            skLineSegment(sketch, "E65.0.1.30", {"start": v(-2438, 8928.83) * mm, "end": v(-2438, 8856.83) * mm});
            skLineSegment(sketch, "E65.0.1.31", {"start": v(-2437, 8928.83) * mm, "end": v(-2437, 8856.83) * mm});
            skLineSegment(sketch, "E65.0.1.32", {"start": v(-2401, 8162.83) * mm, "end": v(-2437, 8094.83) * mm});
            skLineSegment(sketch, "E65.0.1.33", {"start": v(-2437, 8094.83) * mm, "end": v(-2437, 8022.83) * mm});
            skLineSegment(sketch, "E65.0.1.34", {"start": v(-2401, 8510.83) * mm, "end": v(-2401, 8440.83) * mm});
            skLineSegment(sketch, "E65.0.1.35", {"start": v(-2437, 8650.83) * mm, "end": v(-2437, 8578.83) * mm});
            skLineSegment(sketch, "E65.0.1.36", {"start": v(-2401, 9066.83) * mm, "end": v(-2401, 8996.83) * mm});
            skLineSegment(sketch, "E65.0.1.37", {"start": v(-2437, 8300.83) * mm, "end": v(-2401, 8232.83) * mm});
            skLineSegment(sketch, "E65.0.1.38", {"start": v(-2402, 8718.83) * mm, "end": v(-2438, 8650.83) * mm});
            skLineSegment(sketch, "E65.0.1.39", {"start": v(-2437, 8578.83) * mm, "end": v(-2401, 8510.83) * mm});
            skLineSegment(sketch, "E65.0.1.40", {"start": v(-2438, 8372.83) * mm, "end": v(-2438, 8300.83) * mm});
            skLineSegment(sketch, "E65.0.1.41", {"start": v(-2402, 8440.83) * mm, "end": v(-2438, 8372.83) * mm});
            skLineSegment(sketch, "E65.0.1.42", {"start": v(-2438, 8650.83) * mm, "end": v(-2438, 8578.83) * mm});
            skLineSegment(sketch, "E65.0.1.43", {"start": v(-2402, 9066.83) * mm, "end": v(-2402, 8996.83) * mm});
            skLineSegment(sketch, "E65.0.1.44", {"start": v(-2401, 8718.83) * mm, "end": v(-2437, 8650.83) * mm});
            skLineSegment(sketch, "E65.0.1.45", {"start": v(-2401, 8996.83) * mm, "end": v(-2437, 8928.83) * mm});
            skLineSegment(sketch, "E65.0.1.46", {"start": v(-2437, 9134.83) * mm, "end": v(-2401, 9066.83) * mm});
            skLineSegment(sketch, "E65.0.1.47", {"start": v(-2437, 8372.83) * mm, "end": v(-2437, 8300.83) * mm});
            skLineSegment(sketch, "E65.0.1.48", {"start": v(-2401, 8788.83) * mm, "end": v(-2401, 8718.83) * mm});
            skLineSegment(sketch, "E65.0.1.49", {"start": v(-2401, 8232.83) * mm, "end": v(-2401, 8162.83) * mm});
            skLineSegment(sketch, "E65.0.1.50", {"start": v(-2402, 8788.83) * mm, "end": v(-2402, 8718.83) * mm});
            skLineSegment(sketch, "E65.0.1.51", {"start": v(-2438, 9134.83) * mm, "end": v(-2402, 9066.83) * mm});
            skLineSegment(sketch, "E65.0.1.52", {"start": v(-2402, 8996.83) * mm, "end": v(-2438, 8928.83) * mm});
            skLineSegment(sketch, "E65.0.1.53", {"start": v(-2402, 8232.83) * mm, "end": v(-2402, 8162.83) * mm});
            skLineSegment(sketch, "E65.0.1.54", {"start": v(-2402, 8510.83) * mm, "end": v(-2402, 8440.83) * mm});
            skLineSegment(sketch, "E65.0.1.55", {"start": v(-2438, 8300.83) * mm, "end": v(-2402, 8232.83) * mm});
            skLineSegment(sketch, "E65.0.1.56", {"start": v(-2438, 8578.83) * mm, "end": v(-2402, 8510.83) * mm});
            skLineSegment(sketch, "E65.0.1.57", {"start": v(-2401, 8440.83) * mm, "end": v(-2437, 8372.83) * mm});
            skLineSegment(sketch, "E65.0.2.0", {"start": v(-2438, 7466.83) * mm, "end": v(-2402, 7398.83) * mm});
            skLineSegment(sketch, "E65.0.2.1", {"start": v(-2437, 7466.83) * mm, "end": v(-2401, 7398.83) * mm});
            skLineSegment(sketch, "E65.0.2.2", {"start": v(-2438, 7538.83) * mm, "end": v(-2438, 7466.83) * mm});
            skLineSegment(sketch, "E65.0.2.3", {"start": v(-2438, 7816.83) * mm, "end": v(-2438, 7744.83) * mm});
            skLineSegment(sketch, "E65.0.2.4", {"start": v(-2401, 7606.83) * mm, "end": v(-2437, 7538.83) * mm});
            skLineSegment(sketch, "E65.0.2.5", {"start": v(-2401, 7676.83) * mm, "end": v(-2401, 7606.83) * mm});
            skLineSegment(sketch, "E65.0.2.6", {"start": v(-2401, 7328.83) * mm, "end": v(-2437, 7260.83) * mm});
            skLineSegment(sketch, "E65.0.2.7", {"start": v(-2437, 7744.83) * mm, "end": v(-2401, 7676.83) * mm});
            skLineSegment(sketch, "E65.0.2.8", {"start": v(-2402, 7328.83) * mm, "end": v(-2438, 7260.83) * mm});
            skLineSegment(sketch, "E65.0.2.9", {"start": v(-2402, 7676.83) * mm, "end": v(-2402, 7606.83) * mm});
            skLineSegment(sketch, "E65.0.2.10", {"start": v(-2401, 7954.83) * mm, "end": v(-2401, 7884.83) * mm});
            skLineSegment(sketch, "E65.0.2.11", {"start": v(-2402, 7398.83) * mm, "end": v(-2402, 7328.83) * mm});
            skLineSegment(sketch, "E65.0.2.12", {"start": v(-2437, 7538.83) * mm, "end": v(-2437, 7466.83) * mm});
            skLineSegment(sketch, "E65.0.2.13", {"start": v(-2401, 7884.83) * mm, "end": v(-2437, 7816.83) * mm});
            skLineSegment(sketch, "E65.0.2.14", {"start": v(-2402, 7884.83) * mm, "end": v(-2438, 7816.83) * mm});
            skLineSegment(sketch, "E65.0.2.15", {"start": v(-2438, 7260.83) * mm, "end": v(-2438, 7188.83) * mm});
            skLineSegment(sketch, "E65.0.2.16", {"start": v(-2438, 7744.83) * mm, "end": v(-2402, 7676.83) * mm});
            skLineSegment(sketch, "E65.0.2.17", {"start": v(-2402, 7954.83) * mm, "end": v(-2402, 7884.83) * mm});
            skLineSegment(sketch, "E65.0.2.18", {"start": v(-2437, 7816.83) * mm, "end": v(-2437, 7744.83) * mm});
            skLineSegment(sketch, "E65.0.2.19", {"start": v(-2402, 7606.83) * mm, "end": v(-2438, 7538.83) * mm});
            skLineSegment(sketch, "E65.0.2.20", {"start": v(-2437, 7260.83) * mm, "end": v(-2437, 7188.83) * mm});
            skLineSegment(sketch, "E65.0.2.21", {"start": v(-2401, 7398.83) * mm, "end": v(-2401, 7328.83) * mm});
            skLineSegment(sketch, "E65.0.2.22", {"start": v(-2402, 6494.83) * mm, "end": v(-2402, 6216.83) * mm, "construction": true});
            skLineSegment(sketch, "E65.0.2.23", {"start": v(-2438, 6076.83) * mm, "end": v(-2402, 6008.83) * mm});
            skLineSegment(sketch, "E65.0.2.24", {"start": v(-2437, 6076.83) * mm, "end": v(-2401, 6008.83) * mm});
            skLineSegment(sketch, "E65.0.2.25", {"start": v(-2401, 6494.83) * mm, "end": v(-2401, 6216.83) * mm, "construction": true});
            skLineSegment(sketch, "E65.0.2.26", {"start": v(-2437, 6910.83) * mm, "end": v(-2401, 6842.83) * mm});
            skLineSegment(sketch, "E65.0.2.27", {"start": v(-2438, 6910.83) * mm, "end": v(-2402, 6842.83) * mm});
            skLineSegment(sketch, "E65.0.2.28", {"start": v(-2438, 6148.83) * mm, "end": v(-2438, 6076.83) * mm});
            skLineSegment(sketch, "E65.0.2.29", {"start": v(-2402, 6216.83) * mm, "end": v(-2438, 6148.83) * mm});
            skLineSegment(sketch, "E65.0.2.30", {"start": v(-2438, 6982.83) * mm, "end": v(-2438, 6910.83) * mm});
            skLineSegment(sketch, "E65.0.2.31", {"start": v(-2437, 6982.83) * mm, "end": v(-2437, 6910.83) * mm});
            skLineSegment(sketch, "E65.0.2.32", {"start": v(-2401, 6216.83) * mm, "end": v(-2437, 6148.83) * mm});
            skLineSegment(sketch, "E65.0.2.33", {"start": v(-2437, 6148.83) * mm, "end": v(-2437, 6076.83) * mm});
            skLineSegment(sketch, "E65.0.2.34", {"start": v(-2401, 6564.83) * mm, "end": v(-2401, 6494.83) * mm});
            skLineSegment(sketch, "E65.0.2.35", {"start": v(-2437, 6704.83) * mm, "end": v(-2437, 6632.83) * mm});
            skLineSegment(sketch, "E65.0.2.36", {"start": v(-2401, 7120.83) * mm, "end": v(-2401, 7050.83) * mm});
            skLineSegment(sketch, "E65.0.2.37", {"start": v(-2437, 6354.83) * mm, "end": v(-2401, 6286.83) * mm});
            skLineSegment(sketch, "E65.0.2.38", {"start": v(-2402, 6772.83) * mm, "end": v(-2438, 6704.83) * mm});
            skLineSegment(sketch, "E65.0.2.39", {"start": v(-2437, 6632.83) * mm, "end": v(-2401, 6564.83) * mm});
            skLineSegment(sketch, "E65.0.2.40", {"start": v(-2438, 6426.83) * mm, "end": v(-2438, 6354.83) * mm});
            skLineSegment(sketch, "E65.0.2.41", {"start": v(-2402, 6494.83) * mm, "end": v(-2438, 6426.83) * mm});
            skLineSegment(sketch, "E65.0.2.42", {"start": v(-2438, 6704.83) * mm, "end": v(-2438, 6632.83) * mm});
            skLineSegment(sketch, "E65.0.2.43", {"start": v(-2402, 7120.83) * mm, "end": v(-2402, 7050.83) * mm});
            skLineSegment(sketch, "E65.0.2.44", {"start": v(-2401, 6772.83) * mm, "end": v(-2437, 6704.83) * mm});
            skLineSegment(sketch, "E65.0.2.45", {"start": v(-2401, 7050.83) * mm, "end": v(-2437, 6982.83) * mm});
            skLineSegment(sketch, "E65.0.2.46", {"start": v(-2437, 7188.83) * mm, "end": v(-2401, 7120.83) * mm});
            skLineSegment(sketch, "E65.0.2.47", {"start": v(-2437, 6426.83) * mm, "end": v(-2437, 6354.83) * mm});
            skLineSegment(sketch, "E65.0.2.48", {"start": v(-2401, 6842.83) * mm, "end": v(-2401, 6772.83) * mm});
            skLineSegment(sketch, "E65.0.2.49", {"start": v(-2401, 6286.83) * mm, "end": v(-2401, 6216.83) * mm});
            skLineSegment(sketch, "E65.0.2.50", {"start": v(-2402, 6842.83) * mm, "end": v(-2402, 6772.83) * mm});
            skLineSegment(sketch, "E65.0.2.51", {"start": v(-2438, 7188.83) * mm, "end": v(-2402, 7120.83) * mm});
            skLineSegment(sketch, "E65.0.2.52", {"start": v(-2402, 7050.83) * mm, "end": v(-2438, 6982.83) * mm});
            skLineSegment(sketch, "E65.0.2.53", {"start": v(-2402, 6286.83) * mm, "end": v(-2402, 6216.83) * mm});
            skLineSegment(sketch, "E65.0.2.54", {"start": v(-2402, 6564.83) * mm, "end": v(-2402, 6494.83) * mm});
            skLineSegment(sketch, "E65.0.2.55", {"start": v(-2438, 6354.83) * mm, "end": v(-2402, 6286.83) * mm});
            skLineSegment(sketch, "E65.0.2.56", {"start": v(-2438, 6632.83) * mm, "end": v(-2402, 6564.83) * mm});
            skLineSegment(sketch, "E65.0.2.57", {"start": v(-2401, 6494.83) * mm, "end": v(-2437, 6426.83) * mm});
            skLineSegment(sketch, "E65.0.3.0", {"start": v(-2438, 5520.83) * mm, "end": v(-2402, 5452.83) * mm});
            skLineSegment(sketch, "E65.0.3.1", {"start": v(-2437, 5520.83) * mm, "end": v(-2401, 5452.83) * mm});
            skLineSegment(sketch, "E65.0.3.2", {"start": v(-2438, 5592.83) * mm, "end": v(-2438, 5520.83) * mm});
            skLineSegment(sketch, "E65.0.3.3", {"start": v(-2438, 5870.83) * mm, "end": v(-2438, 5798.83) * mm});
            skLineSegment(sketch, "E65.0.3.4", {"start": v(-2401, 5660.83) * mm, "end": v(-2437, 5592.83) * mm});
            skLineSegment(sketch, "E65.0.3.5", {"start": v(-2401, 5730.83) * mm, "end": v(-2401, 5660.83) * mm});
            skLineSegment(sketch, "E65.0.3.6", {"start": v(-2401, 5382.83) * mm, "end": v(-2437, 5314.83) * mm});
            skLineSegment(sketch, "E65.0.3.7", {"start": v(-2437, 5798.83) * mm, "end": v(-2401, 5730.83) * mm});
            skLineSegment(sketch, "E65.0.3.8", {"start": v(-2402, 5382.83) * mm, "end": v(-2438, 5314.83) * mm});
            skLineSegment(sketch, "E65.0.3.9", {"start": v(-2402, 5730.83) * mm, "end": v(-2402, 5660.83) * mm});
            skLineSegment(sketch, "E65.0.3.10", {"start": v(-2401, 6008.83) * mm, "end": v(-2401, 5938.83) * mm});
            skLineSegment(sketch, "E65.0.3.11", {"start": v(-2402, 5452.83) * mm, "end": v(-2402, 5382.83) * mm});
            skLineSegment(sketch, "E65.0.3.12", {"start": v(-2437, 5592.83) * mm, "end": v(-2437, 5520.83) * mm});
            skLineSegment(sketch, "E65.0.3.13", {"start": v(-2401, 5938.83) * mm, "end": v(-2437, 5870.83) * mm});
            skLineSegment(sketch, "E65.0.3.14", {"start": v(-2402, 5938.83) * mm, "end": v(-2438, 5870.83) * mm});
            skLineSegment(sketch, "E65.0.3.15", {"start": v(-2438, 5314.83) * mm, "end": v(-2438, 5242.83) * mm});
            skLineSegment(sketch, "E65.0.3.16", {"start": v(-2438, 5798.83) * mm, "end": v(-2402, 5730.83) * mm});
            skLineSegment(sketch, "E65.0.3.17", {"start": v(-2402, 6008.83) * mm, "end": v(-2402, 5938.83) * mm});
            skLineSegment(sketch, "E65.0.3.18", {"start": v(-2437, 5870.83) * mm, "end": v(-2437, 5798.83) * mm});
            skLineSegment(sketch, "E65.0.3.19", {"start": v(-2402, 5660.83) * mm, "end": v(-2438, 5592.83) * mm});
            skLineSegment(sketch, "E65.0.3.20", {"start": v(-2437, 5314.83) * mm, "end": v(-2437, 5242.83) * mm});
            skLineSegment(sketch, "E65.0.3.21", {"start": v(-2401, 5452.83) * mm, "end": v(-2401, 5382.83) * mm});
            skLineSegment(sketch, "E65.0.3.22", {"start": v(-2402, 4548.83) * mm, "end": v(-2402, 4270.83) * mm, "construction": true});
            skLineSegment(sketch, "E65.0.3.23", {"start": v(-2438, 4130.83) * mm, "end": v(-2402, 4062.83) * mm});
            skLineSegment(sketch, "E65.0.3.24", {"start": v(-2437, 4130.83) * mm, "end": v(-2401, 4062.83) * mm});
            skLineSegment(sketch, "E65.0.3.25", {"start": v(-2401, 4548.83) * mm, "end": v(-2401, 4270.83) * mm, "construction": true});
            skLineSegment(sketch, "E65.0.3.26", {"start": v(-2437, 4964.83) * mm, "end": v(-2401, 4896.83) * mm});
            skLineSegment(sketch, "E65.0.3.27", {"start": v(-2438, 4964.83) * mm, "end": v(-2402, 4896.83) * mm});
            skLineSegment(sketch, "E65.0.3.28", {"start": v(-2438, 4202.83) * mm, "end": v(-2438, 4130.83) * mm});
            skLineSegment(sketch, "E65.0.3.29", {"start": v(-2402, 4270.83) * mm, "end": v(-2438, 4202.83) * mm});
            skLineSegment(sketch, "E65.0.3.30", {"start": v(-2438, 5036.83) * mm, "end": v(-2438, 4964.83) * mm});
            skLineSegment(sketch, "E65.0.3.31", {"start": v(-2437, 5036.83) * mm, "end": v(-2437, 4964.83) * mm});
            skLineSegment(sketch, "E65.0.3.32", {"start": v(-2401, 4270.83) * mm, "end": v(-2437, 4202.83) * mm});
            skLineSegment(sketch, "E65.0.3.33", {"start": v(-2437, 4202.83) * mm, "end": v(-2437, 4130.83) * mm});
            skLineSegment(sketch, "E65.0.3.34", {"start": v(-2401, 4618.83) * mm, "end": v(-2401, 4548.83) * mm});
            skLineSegment(sketch, "E65.0.3.35", {"start": v(-2437, 4758.83) * mm, "end": v(-2437, 4686.83) * mm});
            skLineSegment(sketch, "E65.0.3.36", {"start": v(-2401, 5174.83) * mm, "end": v(-2401, 5104.83) * mm});
            skLineSegment(sketch, "E65.0.3.37", {"start": v(-2437, 4408.83) * mm, "end": v(-2401, 4340.83) * mm});
            skLineSegment(sketch, "E65.0.3.38", {"start": v(-2402, 4826.83) * mm, "end": v(-2438, 4758.83) * mm});
            skLineSegment(sketch, "E65.0.3.39", {"start": v(-2437, 4686.83) * mm, "end": v(-2401, 4618.83) * mm});
            skLineSegment(sketch, "E65.0.3.40", {"start": v(-2438, 4480.83) * mm, "end": v(-2438, 4408.83) * mm});
            skLineSegment(sketch, "E65.0.3.41", {"start": v(-2402, 4548.83) * mm, "end": v(-2438, 4480.83) * mm});
            skLineSegment(sketch, "E65.0.3.42", {"start": v(-2438, 4758.83) * mm, "end": v(-2438, 4686.83) * mm});
            skLineSegment(sketch, "E65.0.3.43", {"start": v(-2402, 5174.83) * mm, "end": v(-2402, 5104.83) * mm});
            skLineSegment(sketch, "E65.0.3.44", {"start": v(-2401, 4826.83) * mm, "end": v(-2437, 4758.83) * mm});
            skLineSegment(sketch, "E65.0.3.45", {"start": v(-2401, 5104.83) * mm, "end": v(-2437, 5036.83) * mm});
            skLineSegment(sketch, "E65.0.3.46", {"start": v(-2437, 5242.83) * mm, "end": v(-2401, 5174.83) * mm});
            skLineSegment(sketch, "E65.0.3.47", {"start": v(-2437, 4480.83) * mm, "end": v(-2437, 4408.83) * mm});
            skLineSegment(sketch, "E65.0.3.48", {"start": v(-2401, 4896.83) * mm, "end": v(-2401, 4826.83) * mm});
            skLineSegment(sketch, "E65.0.3.49", {"start": v(-2401, 4340.83) * mm, "end": v(-2401, 4270.83) * mm});
            skLineSegment(sketch, "E65.0.3.50", {"start": v(-2402, 4896.83) * mm, "end": v(-2402, 4826.83) * mm});
            skLineSegment(sketch, "E65.0.3.51", {"start": v(-2438, 5242.83) * mm, "end": v(-2402, 5174.83) * mm});
            skLineSegment(sketch, "E65.0.3.52", {"start": v(-2402, 5104.83) * mm, "end": v(-2438, 5036.83) * mm});
            skLineSegment(sketch, "E65.0.3.53", {"start": v(-2402, 4340.83) * mm, "end": v(-2402, 4270.83) * mm});
            skLineSegment(sketch, "E65.0.3.54", {"start": v(-2402, 4618.83) * mm, "end": v(-2402, 4548.83) * mm});
            skLineSegment(sketch, "E65.0.3.55", {"start": v(-2438, 4408.83) * mm, "end": v(-2402, 4340.83) * mm});
            skLineSegment(sketch, "E65.0.3.56", {"start": v(-2438, 4686.83) * mm, "end": v(-2402, 4618.83) * mm});
            skLineSegment(sketch, "E65.0.3.57", {"start": v(-2401, 4548.83) * mm, "end": v(-2437, 4480.83) * mm});
            skLineSegment(sketch, "E65.0.4.0", {"start": v(-2438, 3574.83) * mm, "end": v(-2402, 3506.83) * mm});
            skLineSegment(sketch, "E65.0.4.1", {"start": v(-2437, 3574.83) * mm, "end": v(-2401, 3506.83) * mm});
            skLineSegment(sketch, "E65.0.4.2", {"start": v(-2438, 3646.83) * mm, "end": v(-2438, 3574.83) * mm});
            skLineSegment(sketch, "E65.0.4.3", {"start": v(-2438, 3924.83) * mm, "end": v(-2438, 3852.83) * mm});
            skLineSegment(sketch, "E65.0.4.4", {"start": v(-2401, 3714.83) * mm, "end": v(-2437, 3646.83) * mm});
            skLineSegment(sketch, "E65.0.4.5", {"start": v(-2401, 3784.83) * mm, "end": v(-2401, 3714.83) * mm});
            skLineSegment(sketch, "E65.0.4.6", {"start": v(-2401, 3436.83) * mm, "end": v(-2437, 3368.83) * mm});
            skLineSegment(sketch, "E65.0.4.7", {"start": v(-2437, 3852.83) * mm, "end": v(-2401, 3784.83) * mm});
            skLineSegment(sketch, "E65.0.4.8", {"start": v(-2402, 3436.83) * mm, "end": v(-2438, 3368.83) * mm});
            skLineSegment(sketch, "E65.0.4.9", {"start": v(-2402, 3784.83) * mm, "end": v(-2402, 3714.83) * mm});
            skLineSegment(sketch, "E65.0.4.10", {"start": v(-2401, 4062.83) * mm, "end": v(-2401, 3992.83) * mm});
            skLineSegment(sketch, "E65.0.4.11", {"start": v(-2402, 3506.83) * mm, "end": v(-2402, 3436.83) * mm});
            skLineSegment(sketch, "E65.0.4.12", {"start": v(-2437, 3646.83) * mm, "end": v(-2437, 3574.83) * mm});
            skLineSegment(sketch, "E65.0.4.13", {"start": v(-2401, 3992.83) * mm, "end": v(-2437, 3924.83) * mm});
            skLineSegment(sketch, "E65.0.4.14", {"start": v(-2402, 3992.83) * mm, "end": v(-2438, 3924.83) * mm});
            skLineSegment(sketch, "E65.0.4.15", {"start": v(-2438, 3368.83) * mm, "end": v(-2438, 3296.83) * mm});
            skLineSegment(sketch, "E65.0.4.16", {"start": v(-2438, 3852.83) * mm, "end": v(-2402, 3784.83) * mm});
            skLineSegment(sketch, "E65.0.4.17", {"start": v(-2402, 4062.83) * mm, "end": v(-2402, 3992.83) * mm});
            skLineSegment(sketch, "E65.0.4.18", {"start": v(-2437, 3924.83) * mm, "end": v(-2437, 3852.83) * mm});
            skLineSegment(sketch, "E65.0.4.19", {"start": v(-2402, 3714.83) * mm, "end": v(-2438, 3646.83) * mm});
            skLineSegment(sketch, "E65.0.4.20", {"start": v(-2437, 3368.83) * mm, "end": v(-2437, 3296.83) * mm});
            skLineSegment(sketch, "E65.0.4.21", {"start": v(-2401, 3506.83) * mm, "end": v(-2401, 3436.83) * mm});
            skLineSegment(sketch, "E65.0.4.22", {"start": v(-2402, 2602.83) * mm, "end": v(-2402, 2324.83) * mm, "construction": true});
            skLineSegment(sketch, "E65.0.4.23", {"start": v(-2438, 2184.83) * mm, "end": v(-2402, 2116.83) * mm});
            skLineSegment(sketch, "E65.0.4.24", {"start": v(-2437, 2184.83) * mm, "end": v(-2401, 2116.83) * mm});
            skLineSegment(sketch, "E65.0.4.25", {"start": v(-2401, 2602.83) * mm, "end": v(-2401, 2324.83) * mm, "construction": true});
            skLineSegment(sketch, "E65.0.4.26", {"start": v(-2437, 3018.83) * mm, "end": v(-2401, 2950.83) * mm});
            skLineSegment(sketch, "E65.0.4.27", {"start": v(-2438, 3018.83) * mm, "end": v(-2402, 2950.83) * mm});
            skLineSegment(sketch, "E65.0.4.28", {"start": v(-2438, 2256.83) * mm, "end": v(-2438, 2184.83) * mm});
            skLineSegment(sketch, "E65.0.4.29", {"start": v(-2402, 2324.83) * mm, "end": v(-2438, 2256.83) * mm});
            skLineSegment(sketch, "E65.0.4.30", {"start": v(-2438, 3090.83) * mm, "end": v(-2438, 3018.83) * mm});
            skLineSegment(sketch, "E65.0.4.31", {"start": v(-2437, 3090.83) * mm, "end": v(-2437, 3018.83) * mm});
            skLineSegment(sketch, "E65.0.4.32", {"start": v(-2401, 2324.83) * mm, "end": v(-2437, 2256.83) * mm});
            skLineSegment(sketch, "E65.0.4.33", {"start": v(-2437, 2256.83) * mm, "end": v(-2437, 2184.83) * mm});
            skLineSegment(sketch, "E65.0.4.34", {"start": v(-2401, 2672.83) * mm, "end": v(-2401, 2602.83) * mm});
            skLineSegment(sketch, "E65.0.4.35", {"start": v(-2437, 2812.83) * mm, "end": v(-2437, 2740.83) * mm});
            skLineSegment(sketch, "E65.0.4.36", {"start": v(-2401, 3228.83) * mm, "end": v(-2401, 3158.83) * mm});
            skLineSegment(sketch, "E65.0.4.37", {"start": v(-2437, 2462.83) * mm, "end": v(-2401, 2394.83) * mm});
            skLineSegment(sketch, "E65.0.4.38", {"start": v(-2402, 2880.83) * mm, "end": v(-2438, 2812.83) * mm});
            skLineSegment(sketch, "E65.0.4.39", {"start": v(-2437, 2740.83) * mm, "end": v(-2401, 2672.83) * mm});
            skLineSegment(sketch, "E65.0.4.40", {"start": v(-2438, 2534.83) * mm, "end": v(-2438, 2462.83) * mm});
            skLineSegment(sketch, "E65.0.4.41", {"start": v(-2402, 2602.83) * mm, "end": v(-2438, 2534.83) * mm});
            skLineSegment(sketch, "E65.0.4.42", {"start": v(-2438, 2812.83) * mm, "end": v(-2438, 2740.83) * mm});
            skLineSegment(sketch, "E65.0.4.43", {"start": v(-2402, 3228.83) * mm, "end": v(-2402, 3158.83) * mm});
            skLineSegment(sketch, "E65.0.4.44", {"start": v(-2401, 2880.83) * mm, "end": v(-2437, 2812.83) * mm});
            skLineSegment(sketch, "E65.0.4.45", {"start": v(-2401, 3158.83) * mm, "end": v(-2437, 3090.83) * mm});
            skLineSegment(sketch, "E65.0.4.46", {"start": v(-2437, 3296.83) * mm, "end": v(-2401, 3228.83) * mm});
            skLineSegment(sketch, "E65.0.4.47", {"start": v(-2437, 2534.83) * mm, "end": v(-2437, 2462.83) * mm});
            skLineSegment(sketch, "E65.0.4.48", {"start": v(-2401, 2950.83) * mm, "end": v(-2401, 2880.83) * mm});
            skLineSegment(sketch, "E65.0.4.49", {"start": v(-2401, 2394.83) * mm, "end": v(-2401, 2324.83) * mm});
            skLineSegment(sketch, "E65.0.4.50", {"start": v(-2402, 2950.83) * mm, "end": v(-2402, 2880.83) * mm});
            skLineSegment(sketch, "E65.0.4.51", {"start": v(-2438, 3296.83) * mm, "end": v(-2402, 3228.83) * mm});
            skLineSegment(sketch, "E65.0.4.52", {"start": v(-2402, 3158.83) * mm, "end": v(-2438, 3090.83) * mm});
            skLineSegment(sketch, "E65.0.4.53", {"start": v(-2402, 2394.83) * mm, "end": v(-2402, 2324.83) * mm});
            skLineSegment(sketch, "E65.0.4.54", {"start": v(-2402, 2672.83) * mm, "end": v(-2402, 2602.83) * mm});
            skLineSegment(sketch, "E65.0.4.55", {"start": v(-2438, 2462.83) * mm, "end": v(-2402, 2394.83) * mm});
            skLineSegment(sketch, "E65.0.4.56", {"start": v(-2438, 2740.83) * mm, "end": v(-2402, 2672.83) * mm});
            skLineSegment(sketch, "E65.0.4.57", {"start": v(-2401, 2602.83) * mm, "end": v(-2437, 2534.83) * mm});
            skLineSegment(sketch, "E65.0.5.0", {"start": v(-2438, 1628.83) * mm, "end": v(-2402, 1560.83) * mm});
            skLineSegment(sketch, "E65.0.5.1", {"start": v(-2437, 1628.83) * mm, "end": v(-2401, 1560.83) * mm});
            skLineSegment(sketch, "E65.0.5.2", {"start": v(-2438, 1700.83) * mm, "end": v(-2438, 1628.83) * mm});
            skLineSegment(sketch, "E65.0.5.3", {"start": v(-2438, 1978.83) * mm, "end": v(-2438, 1906.83) * mm});
            skLineSegment(sketch, "E65.0.5.4", {"start": v(-2401, 1768.83) * mm, "end": v(-2437, 1700.83) * mm});
            skLineSegment(sketch, "E65.0.5.5", {"start": v(-2401, 1838.83) * mm, "end": v(-2401, 1768.83) * mm});
            skLineSegment(sketch, "E65.0.5.6", {"start": v(-2401, 1490.83) * mm, "end": v(-2437, 1422.83) * mm});
            skLineSegment(sketch, "E65.0.5.7", {"start": v(-2437, 1906.83) * mm, "end": v(-2401, 1838.83) * mm});
            skLineSegment(sketch, "E65.0.5.8", {"start": v(-2402, 1490.83) * mm, "end": v(-2438, 1422.83) * mm});
            skLineSegment(sketch, "E65.0.5.9", {"start": v(-2402, 1838.83) * mm, "end": v(-2402, 1768.83) * mm});
            skLineSegment(sketch, "E65.0.5.10", {"start": v(-2401, 2116.83) * mm, "end": v(-2401, 2046.83) * mm});
            skLineSegment(sketch, "E65.0.5.11", {"start": v(-2402, 1560.83) * mm, "end": v(-2402, 1490.83) * mm});
            skLineSegment(sketch, "E65.0.5.12", {"start": v(-2437, 1700.83) * mm, "end": v(-2437, 1628.83) * mm});
            skLineSegment(sketch, "E65.0.5.13", {"start": v(-2401, 2046.83) * mm, "end": v(-2437, 1978.83) * mm});
            skLineSegment(sketch, "E65.0.5.14", {"start": v(-2402, 2046.83) * mm, "end": v(-2438, 1978.83) * mm});
            skLineSegment(sketch, "E65.0.5.15", {"start": v(-2438, 1422.83) * mm, "end": v(-2438, 1350.83) * mm});
            skLineSegment(sketch, "E65.0.5.16", {"start": v(-2438, 1906.83) * mm, "end": v(-2402, 1838.83) * mm});
            skLineSegment(sketch, "E65.0.5.17", {"start": v(-2402, 2116.83) * mm, "end": v(-2402, 2046.83) * mm});
            skLineSegment(sketch, "E65.0.5.18", {"start": v(-2437, 1978.83) * mm, "end": v(-2437, 1906.83) * mm});
            skLineSegment(sketch, "E65.0.5.19", {"start": v(-2402, 1768.83) * mm, "end": v(-2438, 1700.83) * mm});
            skLineSegment(sketch, "E65.0.5.20", {"start": v(-2437, 1422.83) * mm, "end": v(-2437, 1350.83) * mm});
            skLineSegment(sketch, "E65.0.5.21", {"start": v(-2401, 1560.83) * mm, "end": v(-2401, 1490.83) * mm});
            skLineSegment(sketch, "E65.0.5.22", {"start": v(-2402, 656.83) * mm, "end": v(-2402, 378.83) * mm, "construction": true});
            skLineSegment(sketch, "E65.0.5.23", {"start": v(-2438, 238.83) * mm, "end": v(-2402, 170.83) * mm});
            skLineSegment(sketch, "E65.0.5.24", {"start": v(-2437, 238.83) * mm, "end": v(-2401, 170.83) * mm});
            skLineSegment(sketch, "E65.0.5.25", {"start": v(-2401, 656.83) * mm, "end": v(-2401, 378.83) * mm, "construction": true});
            skLineSegment(sketch, "E65.0.5.26", {"start": v(-2437, 1072.83) * mm, "end": v(-2401, 1004.83) * mm});
            skLineSegment(sketch, "E65.0.5.27", {"start": v(-2438, 1072.83) * mm, "end": v(-2402, 1004.83) * mm});
            skLineSegment(sketch, "E65.0.5.28", {"start": v(-2438, 310.83) * mm, "end": v(-2438, 238.83) * mm});
            skLineSegment(sketch, "E65.0.5.29", {"start": v(-2402, 378.83) * mm, "end": v(-2438, 310.83) * mm});
            skLineSegment(sketch, "E65.0.5.30", {"start": v(-2438, 1144.83) * mm, "end": v(-2438, 1072.83) * mm});
            skLineSegment(sketch, "E65.0.5.31", {"start": v(-2437, 1144.83) * mm, "end": v(-2437, 1072.83) * mm});
            skLineSegment(sketch, "E65.0.5.32", {"start": v(-2401, 378.83) * mm, "end": v(-2437, 310.83) * mm});
            skLineSegment(sketch, "E65.0.5.33", {"start": v(-2437, 310.83) * mm, "end": v(-2437, 238.83) * mm});
            skLineSegment(sketch, "E65.0.5.34", {"start": v(-2401, 726.83) * mm, "end": v(-2401, 656.83) * mm});
            skLineSegment(sketch, "E65.0.5.35", {"start": v(-2437, 866.83) * mm, "end": v(-2437, 794.83) * mm});
            skLineSegment(sketch, "E65.0.5.36", {"start": v(-2401, 1282.83) * mm, "end": v(-2401, 1212.83) * mm});
            skLineSegment(sketch, "E65.0.5.37", {"start": v(-2437, 516.83) * mm, "end": v(-2401, 448.83) * mm});
            skLineSegment(sketch, "E65.0.5.38", {"start": v(-2402, 934.83) * mm, "end": v(-2438, 866.83) * mm});
            skLineSegment(sketch, "E65.0.5.39", {"start": v(-2437, 794.83) * mm, "end": v(-2401, 726.83) * mm});
            skLineSegment(sketch, "E65.0.5.40", {"start": v(-2438, 588.83) * mm, "end": v(-2438, 516.83) * mm});
            skLineSegment(sketch, "E65.0.5.41", {"start": v(-2402, 656.83) * mm, "end": v(-2438, 588.83) * mm});
            skLineSegment(sketch, "E65.0.5.42", {"start": v(-2438, 866.83) * mm, "end": v(-2438, 794.83) * mm});
            skLineSegment(sketch, "E65.0.5.43", {"start": v(-2402, 1282.83) * mm, "end": v(-2402, 1212.83) * mm});
            skLineSegment(sketch, "E65.0.5.44", {"start": v(-2401, 934.83) * mm, "end": v(-2437, 866.83) * mm});
            skLineSegment(sketch, "E65.0.5.45", {"start": v(-2401, 1212.83) * mm, "end": v(-2437, 1144.83) * mm});
            skLineSegment(sketch, "E65.0.5.46", {"start": v(-2437, 1350.83) * mm, "end": v(-2401, 1282.83) * mm});
            skLineSegment(sketch, "E65.0.5.47", {"start": v(-2437, 588.83) * mm, "end": v(-2437, 516.83) * mm});
            skLineSegment(sketch, "E65.0.5.48", {"start": v(-2401, 1004.83) * mm, "end": v(-2401, 934.83) * mm});
            skLineSegment(sketch, "E65.0.5.49", {"start": v(-2401, 448.83) * mm, "end": v(-2401, 378.83) * mm});
            skLineSegment(sketch, "E65.0.5.50", {"start": v(-2402, 1004.83) * mm, "end": v(-2402, 934.83) * mm});
            skLineSegment(sketch, "E65.0.5.51", {"start": v(-2438, 1350.83) * mm, "end": v(-2402, 1282.83) * mm});
            skLineSegment(sketch, "E65.0.5.52", {"start": v(-2402, 1212.83) * mm, "end": v(-2438, 1144.83) * mm});
            skLineSegment(sketch, "E65.0.5.53", {"start": v(-2402, 448.83) * mm, "end": v(-2402, 378.83) * mm});
            skLineSegment(sketch, "E65.0.5.54", {"start": v(-2402, 726.83) * mm, "end": v(-2402, 656.83) * mm});
            skLineSegment(sketch, "E65.0.5.55", {"start": v(-2438, 516.83) * mm, "end": v(-2402, 448.83) * mm});
            skLineSegment(sketch, "E65.0.5.56", {"start": v(-2438, 794.83) * mm, "end": v(-2402, 726.83) * mm});
            skLineSegment(sketch, "E65.0.5.57", {"start": v(-2401, 656.83) * mm, "end": v(-2437, 588.83) * mm});
            skLineSegment(sketch, "E65.direction1", {"start": v(-2401, 11846.83) * mm, "end": v(-2426, 11846.83) * mm, "construction": true});
            skLineSegment(sketch, "E65.direction2", {"start": v(-2401, 11846.83) * mm, "end": v(-2401, 9900.83) * mm, "construction": true});
            skLineSegment(sketch, "E66", {"start": v(-2402, 170.83) * mm, "end": v(-2402, 100) * mm});
            skLineSegment(sketch, "E67", {"start": v(-2402, 100) * mm, "end": v(-2401, 100) * mm});
            skLineSegment(sketch, "E68", {"start": v(-2401, 100) * mm, "end": v(-2401, 170.83) * mm});
            skSolve(sketch);
        }
        {
            var Q0;
            Q0 = qSketchRegion(id + "F14", true);
            extrude(context, id + "F15", {"entities" : qUnion([Q0]), "operationType" : NewBodyOperationType.ADD, "depth" : 2696 * mm, "offsetDistance" : 25 * mm});
        }
        {
            var Q0;
            Q0=makeQuery(id+"F7.boolean.opBoolean","COPY",FACE,{"derivedFrom":makeQuery(id+"F7.opExtrude","SWEPT_FACE",FACE,{"disambiguationData":[OSD([sQuery(id+"F6.wireOp",EDGE,"E12")])]})});
            var sketch = newSketch(context, id + "F16", { "sketchPlane" : qUnion([Q0])});
            skLineSegment(sketch, "E69", {"start": v(12091.83, 2859.97) * mm, "end": v(12054.83, 2859.97) * mm});
            skLineSegment(sketch, "E70", {"start": v(11986.83, 2895.97) * mm, "end": v(11914.83, 2895.97) * mm});
            skLineSegment(sketch, "E71", {"start": v(11846.83, 2859.97) * mm, "end": v(11776.83, 2859.97) * mm});
            skLineSegment(sketch, "E72", {"start": v(12054.83, 2859.97) * mm, "end": v(11986.83, 2895.97) * mm});
            skLineSegment(sketch, "E73", {"start": v(11914.83, 2895.97) * mm, "end": v(11846.83, 2859.97) * mm});
            skLineSegment(sketch, "E74.1.0.0", {"start": v(11776.83, 2859.97) * mm, "end": v(11708.83, 2895.97) * mm});
            skLineSegment(sketch, "E74.1.0.1", {"start": v(11708.83, 2895.97) * mm, "end": v(11636.83, 2895.97) * mm});
            skLineSegment(sketch, "E74.1.0.2", {"start": v(11636.83, 2895.97) * mm, "end": v(11568.83, 2859.97) * mm});
            skLineSegment(sketch, "E74.1.0.3", {"start": v(11568.83, 2859.97) * mm, "end": v(11498.83, 2859.97) * mm});
            skLineSegment(sketch, "E74.2.0.0", {"start": v(11498.83, 2859.97) * mm, "end": v(11430.83, 2895.97) * mm});
            skLineSegment(sketch, "E74.2.0.1", {"start": v(11430.83, 2895.97) * mm, "end": v(11358.83, 2895.97) * mm});
            skLineSegment(sketch, "E74.2.0.2", {"start": v(11358.83, 2895.97) * mm, "end": v(11290.83, 2859.97) * mm});
            skLineSegment(sketch, "E74.2.0.3", {"start": v(11290.83, 2859.97) * mm, "end": v(11220.83, 2859.97) * mm});
            skLineSegment(sketch, "E74.3.0.0", {"start": v(11220.83, 2859.97) * mm, "end": v(11152.83, 2895.97) * mm});
            skLineSegment(sketch, "E74.3.0.1", {"start": v(11152.83, 2895.97) * mm, "end": v(11080.83, 2895.97) * mm});
            skLineSegment(sketch, "E74.3.0.2", {"start": v(11080.83, 2895.97) * mm, "end": v(11012.83, 2859.97) * mm});
            skLineSegment(sketch, "E74.3.0.3", {"start": v(11012.83, 2859.97) * mm, "end": v(10942.83, 2859.97) * mm});
            skLineSegment(sketch, "E74.4.0.0", {"start": v(10942.83, 2859.97) * mm, "end": v(10874.83, 2895.97) * mm});
            skLineSegment(sketch, "E74.4.0.1", {"start": v(10874.83, 2895.97) * mm, "end": v(10802.83, 2895.97) * mm});
            skLineSegment(sketch, "E74.4.0.2", {"start": v(10802.83, 2895.97) * mm, "end": v(10734.83, 2859.97) * mm});
            skLineSegment(sketch, "E74.4.0.3", {"start": v(10734.83, 2859.97) * mm, "end": v(10664.83, 2859.97) * mm});
            skLineSegment(sketch, "E74.5.0.0", {"start": v(10664.83, 2859.97) * mm, "end": v(10596.83, 2895.97) * mm});
            skLineSegment(sketch, "E74.5.0.1", {"start": v(10596.83, 2895.97) * mm, "end": v(10524.83, 2895.97) * mm});
            skLineSegment(sketch, "E74.5.0.2", {"start": v(10524.83, 2895.97) * mm, "end": v(10456.83, 2859.97) * mm});
            skLineSegment(sketch, "E74.5.0.3", {"start": v(10456.83, 2859.97) * mm, "end": v(10386.83, 2859.97) * mm});
            skLineSegment(sketch, "E74.6.0.0", {"start": v(10386.83, 2859.97) * mm, "end": v(10318.83, 2895.97) * mm});
            skLineSegment(sketch, "E74.6.0.1", {"start": v(10318.83, 2895.97) * mm, "end": v(10246.83, 2895.97) * mm});
            skLineSegment(sketch, "E74.6.0.2", {"start": v(10246.83, 2895.97) * mm, "end": v(10178.83, 2859.97) * mm});
            skLineSegment(sketch, "E74.6.0.3", {"start": v(10178.83, 2859.97) * mm, "end": v(10108.83, 2859.97) * mm});
            skLineSegment(sketch, "E74.direction1", {"start": v(12054.83, 2859.97) * mm, "end": v(11776.83, 2859.97) * mm, "construction": true});
            skLineSegment(sketch, "E75.1.0.0", {"start": v(10108.83, 2859.97) * mm, "end": v(10040.83, 2895.97) * mm});
            skLineSegment(sketch, "E75.1.0.1", {"start": v(10040.83, 2895.97) * mm, "end": v(9968.83, 2895.97) * mm});
            skLineSegment(sketch, "E75.1.0.2", {"start": v(9968.83, 2895.97) * mm, "end": v(9900.83, 2859.97) * mm});
            skLineSegment(sketch, "E75.direction1", {"start": v(10386.83, 2859.97) * mm, "end": v(10108.83, 2859.97) * mm, "construction": true});
            skLineSegment(sketch, "E76.0.1.0", {"start": v(12054.83, 2858.97) * mm, "end": v(11776.83, 2858.97) * mm, "construction": true});
            skLineSegment(sketch, "E76.0.1.1", {"start": v(10386.83, 2858.97) * mm, "end": v(10108.83, 2858.97) * mm, "construction": true});
            skLineSegment(sketch, "E76.0.1.2", {"start": v(10108.83, 2858.97) * mm, "end": v(10040.83, 2894.97) * mm});
            skLineSegment(sketch, "E76.0.1.3", {"start": v(11012.83, 2858.97) * mm, "end": v(10942.83, 2858.97) * mm});
            skLineSegment(sketch, "E76.0.1.5", {"start": v(11358.83, 2894.97) * mm, "end": v(11290.83, 2858.97) * mm});
            skLineSegment(sketch, "E76.0.1.6", {"start": v(11220.83, 2858.97) * mm, "end": v(11152.83, 2894.97) * mm});
            skLineSegment(sketch, "E76.0.1.7", {"start": v(10802.83, 2894.97) * mm, "end": v(10734.83, 2858.97) * mm});
            skLineSegment(sketch, "E76.0.1.8", {"start": v(10386.83, 2858.97) * mm, "end": v(10318.83, 2894.97) * mm});
            skLineSegment(sketch, "E76.0.1.9", {"start": v(11708.83, 2894.97) * mm, "end": v(11636.83, 2894.97) * mm});
            skLineSegment(sketch, "E76.0.1.10", {"start": v(9968.83, 2894.97) * mm, "end": v(9900.83, 2858.97) * mm});
            skLineSegment(sketch, "E76.0.1.11", {"start": v(10664.83, 2858.97) * mm, "end": v(10596.83, 2894.97) * mm});
            skLineSegment(sketch, "E76.0.1.12", {"start": v(11636.83, 2894.97) * mm, "end": v(11568.83, 2858.97) * mm});
            skLineSegment(sketch, "E76.0.1.13", {"start": v(11776.83, 2858.97) * mm, "end": v(11708.83, 2894.97) * mm});
            skLineSegment(sketch, "E76.0.1.14", {"start": v(10246.83, 2894.97) * mm, "end": v(10178.83, 2858.97) * mm});
            skLineSegment(sketch, "E76.0.1.15", {"start": v(11430.83, 2894.97) * mm, "end": v(11358.83, 2894.97) * mm});
            skLineSegment(sketch, "E76.0.1.16", {"start": v(10942.83, 2858.97) * mm, "end": v(10874.83, 2894.97) * mm});
            skLineSegment(sketch, "E76.0.1.17", {"start": v(11498.83, 2858.97) * mm, "end": v(11430.83, 2894.97) * mm});
            skLineSegment(sketch, "E76.0.1.18", {"start": v(10040.83, 2894.97) * mm, "end": v(9968.83, 2894.97) * mm});
            skLineSegment(sketch, "E76.0.1.19", {"start": v(10734.83, 2858.97) * mm, "end": v(10664.83, 2858.97) * mm});
            skLineSegment(sketch, "E76.0.1.20", {"start": v(10596.83, 2894.97) * mm, "end": v(10524.83, 2894.97) * mm});
            skLineSegment(sketch, "E76.0.1.21", {"start": v(10524.83, 2894.97) * mm, "end": v(10456.83, 2858.97) * mm});
            skLineSegment(sketch, "E76.0.1.22", {"start": v(11568.83, 2858.97) * mm, "end": v(11498.83, 2858.97) * mm});
            skLineSegment(sketch, "E76.0.1.23", {"start": v(10318.83, 2894.97) * mm, "end": v(10246.83, 2894.97) * mm});
            skLineSegment(sketch, "E76.0.1.24", {"start": v(11914.83, 2894.97) * mm, "end": v(11846.83, 2858.97) * mm});
            skLineSegment(sketch, "E76.0.1.25", {"start": v(10874.83, 2894.97) * mm, "end": v(10802.83, 2894.97) * mm});
            skLineSegment(sketch, "E76.0.1.26", {"start": v(12054.83, 2858.97) * mm, "end": v(11986.83, 2894.97) * mm});
            skLineSegment(sketch, "E76.0.1.27", {"start": v(11290.83, 2858.97) * mm, "end": v(11220.83, 2858.97) * mm});
            skLineSegment(sketch, "E76.0.1.28", {"start": v(11152.83, 2894.97) * mm, "end": v(11080.83, 2894.97) * mm});
            skLineSegment(sketch, "E76.0.1.29", {"start": v(11986.83, 2894.97) * mm, "end": v(11914.83, 2894.97) * mm});
            skLineSegment(sketch, "E76.0.1.30", {"start": v(11080.83, 2894.97) * mm, "end": v(11012.83, 2858.97) * mm});
            skLineSegment(sketch, "E76.0.1.31", {"start": v(10178.83, 2858.97) * mm, "end": v(10108.83, 2858.97) * mm});
            skLineSegment(sketch, "E76.0.1.32", {"start": v(11846.83, 2858.97) * mm, "end": v(11776.83, 2858.97) * mm});
            skLineSegment(sketch, "E76.0.1.33", {"start": v(10456.83, 2858.97) * mm, "end": v(10386.83, 2858.97) * mm});
            skLineSegment(sketch, "E76.0.1.34", {"start": v(12091.83, 2858.97) * mm, "end": v(12054.83, 2858.97) * mm});
            skLineSegment(sketch, "E77", {"start": v(12091.83, 2858.97) * mm, "end": v(12092, 2858.97) * mm});
            skLineSegment(sketch, "E78", {"start": v(12092, 2858.97) * mm, "end": v(12092, 2859.97) * mm});
            skLineSegment(sketch, "E79", {"start": v(12092, 2859.97) * mm, "end": v(12091.83, 2859.97) * mm});
            skLineSegment(sketch, "E80.0.1.0", {"start": v(9412.83, 2895.97) * mm, "end": v(9344.83, 2859.97) * mm});
            skLineSegment(sketch, "E80.0.1.1", {"start": v(9412.83, 2894.97) * mm, "end": v(9344.83, 2858.97) * mm});
            skLineSegment(sketch, "E80.0.1.2", {"start": v(9484.83, 2895.97) * mm, "end": v(9412.83, 2895.97) * mm});
            skLineSegment(sketch, "E80.0.1.3", {"start": v(9762.83, 2895.97) * mm, "end": v(9690.83, 2895.97) * mm});
            skLineSegment(sketch, "E80.0.1.4", {"start": v(9552.83, 2858.97) * mm, "end": v(9484.83, 2894.97) * mm});
            skLineSegment(sketch, "E80.0.1.5", {"start": v(9622.83, 2858.97) * mm, "end": v(9552.83, 2858.97) * mm});
            skLineSegment(sketch, "E80.0.1.6", {"start": v(9274.83, 2858.97) * mm, "end": v(9206.83, 2894.97) * mm});
            skLineSegment(sketch, "E80.0.1.7", {"start": v(9690.83, 2894.97) * mm, "end": v(9622.83, 2858.97) * mm});
            skLineSegment(sketch, "E80.0.1.8", {"start": v(9274.83, 2859.97) * mm, "end": v(9206.83, 2895.97) * mm});
            skLineSegment(sketch, "E80.0.1.9", {"start": v(9622.83, 2859.97) * mm, "end": v(9552.83, 2859.97) * mm});
            skLineSegment(sketch, "E80.0.1.10", {"start": v(9900.83, 2858.97) * mm, "end": v(9830.83, 2858.97) * mm});
            skLineSegment(sketch, "E80.0.1.11", {"start": v(9344.83, 2859.97) * mm, "end": v(9274.83, 2859.97) * mm});
            skLineSegment(sketch, "E80.0.1.12", {"start": v(9484.83, 2894.97) * mm, "end": v(9412.83, 2894.97) * mm});
            skLineSegment(sketch, "E80.0.1.13", {"start": v(9830.83, 2858.97) * mm, "end": v(9762.83, 2894.97) * mm});
            skLineSegment(sketch, "E80.0.1.14", {"start": v(9830.83, 2859.97) * mm, "end": v(9762.83, 2895.97) * mm});
            skLineSegment(sketch, "E80.0.1.15", {"start": v(9206.83, 2895.97) * mm, "end": v(9134.83, 2895.97) * mm});
            skLineSegment(sketch, "E80.0.1.16", {"start": v(9690.83, 2895.97) * mm, "end": v(9622.83, 2859.97) * mm});
            skLineSegment(sketch, "E80.0.1.17", {"start": v(9900.83, 2859.97) * mm, "end": v(9830.83, 2859.97) * mm});
            skLineSegment(sketch, "E80.0.1.18", {"start": v(9762.83, 2894.97) * mm, "end": v(9690.83, 2894.97) * mm});
            skLineSegment(sketch, "E80.0.1.19", {"start": v(9552.83, 2859.97) * mm, "end": v(9484.83, 2895.97) * mm});
            skLineSegment(sketch, "E80.0.1.20", {"start": v(9206.83, 2894.97) * mm, "end": v(9134.83, 2894.97) * mm});
            skLineSegment(sketch, "E80.0.1.21", {"start": v(9344.83, 2858.97) * mm, "end": v(9274.83, 2858.97) * mm});
            skLineSegment(sketch, "E80.0.1.22", {"start": v(8440.83, 2859.97) * mm, "end": v(8162.83, 2859.97) * mm, "construction": true});
            skLineSegment(sketch, "E80.0.1.23", {"start": v(8022.83, 2895.97) * mm, "end": v(7954.83, 2859.97) * mm});
            skLineSegment(sketch, "E80.0.1.24", {"start": v(8022.83, 2894.97) * mm, "end": v(7954.83, 2858.97) * mm});
            skLineSegment(sketch, "E80.0.1.25", {"start": v(8440.83, 2858.97) * mm, "end": v(8162.83, 2858.97) * mm, "construction": true});
            skLineSegment(sketch, "E80.0.1.26", {"start": v(8856.83, 2894.97) * mm, "end": v(8788.83, 2858.97) * mm});
            skLineSegment(sketch, "E80.0.1.27", {"start": v(8856.83, 2895.97) * mm, "end": v(8788.83, 2859.97) * mm});
            skLineSegment(sketch, "E80.0.1.28", {"start": v(8094.83, 2895.97) * mm, "end": v(8022.83, 2895.97) * mm});
            skLineSegment(sketch, "E80.0.1.29", {"start": v(8162.83, 2859.97) * mm, "end": v(8094.83, 2895.97) * mm});
            skLineSegment(sketch, "E80.0.1.30", {"start": v(8928.83, 2895.97) * mm, "end": v(8856.83, 2895.97) * mm});
            skLineSegment(sketch, "E80.0.1.31", {"start": v(8928.83, 2894.97) * mm, "end": v(8856.83, 2894.97) * mm});
            skLineSegment(sketch, "E80.0.1.32", {"start": v(8162.83, 2858.97) * mm, "end": v(8094.83, 2894.97) * mm});
            skLineSegment(sketch, "E80.0.1.33", {"start": v(8094.83, 2894.97) * mm, "end": v(8022.83, 2894.97) * mm});
            skLineSegment(sketch, "E80.0.1.34", {"start": v(8510.83, 2858.97) * mm, "end": v(8440.83, 2858.97) * mm});
            skLineSegment(sketch, "E80.0.1.35", {"start": v(8650.83, 2894.97) * mm, "end": v(8578.83, 2894.97) * mm});
            skLineSegment(sketch, "E80.0.1.36", {"start": v(9066.83, 2858.97) * mm, "end": v(8996.83, 2858.97) * mm});
            skLineSegment(sketch, "E80.0.1.37", {"start": v(8300.83, 2894.97) * mm, "end": v(8232.83, 2858.97) * mm});
            skLineSegment(sketch, "E80.0.1.38", {"start": v(8718.83, 2859.97) * mm, "end": v(8650.83, 2895.97) * mm});
            skLineSegment(sketch, "E80.0.1.39", {"start": v(8578.83, 2894.97) * mm, "end": v(8510.83, 2858.97) * mm});
            skLineSegment(sketch, "E80.0.1.40", {"start": v(8372.83, 2895.97) * mm, "end": v(8300.83, 2895.97) * mm});
            skLineSegment(sketch, "E80.0.1.41", {"start": v(8440.83, 2859.97) * mm, "end": v(8372.83, 2895.97) * mm});
            skLineSegment(sketch, "E80.0.1.42", {"start": v(8650.83, 2895.97) * mm, "end": v(8578.83, 2895.97) * mm});
            skLineSegment(sketch, "E80.0.1.43", {"start": v(9066.83, 2859.97) * mm, "end": v(8996.83, 2859.97) * mm});
            skLineSegment(sketch, "E80.0.1.44", {"start": v(8718.83, 2858.97) * mm, "end": v(8650.83, 2894.97) * mm});
            skLineSegment(sketch, "E80.0.1.45", {"start": v(8996.83, 2858.97) * mm, "end": v(8928.83, 2894.97) * mm});
            skLineSegment(sketch, "E80.0.1.46", {"start": v(9134.83, 2894.97) * mm, "end": v(9066.83, 2858.97) * mm});
            skLineSegment(sketch, "E80.0.1.47", {"start": v(8372.83, 2894.97) * mm, "end": v(8300.83, 2894.97) * mm});
            skLineSegment(sketch, "E80.0.1.48", {"start": v(8788.83, 2858.97) * mm, "end": v(8718.83, 2858.97) * mm});
            skLineSegment(sketch, "E80.0.1.49", {"start": v(8232.83, 2858.97) * mm, "end": v(8162.83, 2858.97) * mm});
            skLineSegment(sketch, "E80.0.1.50", {"start": v(8788.83, 2859.97) * mm, "end": v(8718.83, 2859.97) * mm});
            skLineSegment(sketch, "E80.0.1.51", {"start": v(9134.83, 2895.97) * mm, "end": v(9066.83, 2859.97) * mm});
            skLineSegment(sketch, "E80.0.1.52", {"start": v(8996.83, 2859.97) * mm, "end": v(8928.83, 2895.97) * mm});
            skLineSegment(sketch, "E80.0.1.53", {"start": v(8232.83, 2859.97) * mm, "end": v(8162.83, 2859.97) * mm});
            skLineSegment(sketch, "E80.0.1.54", {"start": v(8510.83, 2859.97) * mm, "end": v(8440.83, 2859.97) * mm});
            skLineSegment(sketch, "E80.0.1.55", {"start": v(8300.83, 2895.97) * mm, "end": v(8232.83, 2859.97) * mm});
            skLineSegment(sketch, "E80.0.1.56", {"start": v(8578.83, 2895.97) * mm, "end": v(8510.83, 2859.97) * mm});
            skLineSegment(sketch, "E80.0.1.57", {"start": v(8440.83, 2858.97) * mm, "end": v(8372.83, 2894.97) * mm});
            skLineSegment(sketch, "E80.0.2.0", {"start": v(7466.83, 2895.97) * mm, "end": v(7398.83, 2859.97) * mm});
            skLineSegment(sketch, "E80.0.2.1", {"start": v(7466.83, 2894.97) * mm, "end": v(7398.83, 2858.97) * mm});
            skLineSegment(sketch, "E80.0.2.2", {"start": v(7538.83, 2895.97) * mm, "end": v(7466.83, 2895.97) * mm});
            skLineSegment(sketch, "E80.0.2.3", {"start": v(7816.83, 2895.97) * mm, "end": v(7744.83, 2895.97) * mm});
            skLineSegment(sketch, "E80.0.2.4", {"start": v(7606.83, 2858.97) * mm, "end": v(7538.83, 2894.97) * mm});
            skLineSegment(sketch, "E80.0.2.5", {"start": v(7676.83, 2858.97) * mm, "end": v(7606.83, 2858.97) * mm});
            skLineSegment(sketch, "E80.0.2.6", {"start": v(7328.83, 2858.97) * mm, "end": v(7260.83, 2894.97) * mm});
            skLineSegment(sketch, "E80.0.2.7", {"start": v(7744.83, 2894.97) * mm, "end": v(7676.83, 2858.97) * mm});
            skLineSegment(sketch, "E80.0.2.8", {"start": v(7328.83, 2859.97) * mm, "end": v(7260.83, 2895.97) * mm});
            skLineSegment(sketch, "E80.0.2.9", {"start": v(7676.83, 2859.97) * mm, "end": v(7606.83, 2859.97) * mm});
            skLineSegment(sketch, "E80.0.2.10", {"start": v(7954.83, 2858.97) * mm, "end": v(7884.83, 2858.97) * mm});
            skLineSegment(sketch, "E80.0.2.11", {"start": v(7398.83, 2859.97) * mm, "end": v(7328.83, 2859.97) * mm});
            skLineSegment(sketch, "E80.0.2.12", {"start": v(7538.83, 2894.97) * mm, "end": v(7466.83, 2894.97) * mm});
            skLineSegment(sketch, "E80.0.2.13", {"start": v(7884.83, 2858.97) * mm, "end": v(7816.83, 2894.97) * mm});
            skLineSegment(sketch, "E80.0.2.14", {"start": v(7884.83, 2859.97) * mm, "end": v(7816.83, 2895.97) * mm});
            skLineSegment(sketch, "E80.0.2.15", {"start": v(7260.83, 2895.97) * mm, "end": v(7188.83, 2895.97) * mm});
            skLineSegment(sketch, "E80.0.2.16", {"start": v(7744.83, 2895.97) * mm, "end": v(7676.83, 2859.97) * mm});
            skLineSegment(sketch, "E80.0.2.17", {"start": v(7954.83, 2859.97) * mm, "end": v(7884.83, 2859.97) * mm});
            skLineSegment(sketch, "E80.0.2.18", {"start": v(7816.83, 2894.97) * mm, "end": v(7744.83, 2894.97) * mm});
            skLineSegment(sketch, "E80.0.2.19", {"start": v(7606.83, 2859.97) * mm, "end": v(7538.83, 2895.97) * mm});
            skLineSegment(sketch, "E80.0.2.20", {"start": v(7260.83, 2894.97) * mm, "end": v(7188.83, 2894.97) * mm});
            skLineSegment(sketch, "E80.0.2.21", {"start": v(7398.83, 2858.97) * mm, "end": v(7328.83, 2858.97) * mm});
            skLineSegment(sketch, "E80.0.2.22", {"start": v(6494.83, 2859.97) * mm, "end": v(6216.83, 2859.97) * mm, "construction": true});
            skLineSegment(sketch, "E80.0.2.23", {"start": v(6076.83, 2895.97) * mm, "end": v(6008.83, 2859.97) * mm});
            skLineSegment(sketch, "E80.0.2.24", {"start": v(6076.83, 2894.97) * mm, "end": v(6008.83, 2858.97) * mm});
            skLineSegment(sketch, "E80.0.2.25", {"start": v(6494.83, 2858.97) * mm, "end": v(6216.83, 2858.97) * mm, "construction": true});
            skLineSegment(sketch, "E80.0.2.26", {"start": v(6910.83, 2894.97) * mm, "end": v(6842.83, 2858.97) * mm});
            skLineSegment(sketch, "E80.0.2.27", {"start": v(6910.83, 2895.97) * mm, "end": v(6842.83, 2859.97) * mm});
            skLineSegment(sketch, "E80.0.2.28", {"start": v(6148.83, 2895.97) * mm, "end": v(6076.83, 2895.97) * mm});
            skLineSegment(sketch, "E80.0.2.29", {"start": v(6216.83, 2859.97) * mm, "end": v(6148.83, 2895.97) * mm});
            skLineSegment(sketch, "E80.0.2.30", {"start": v(6982.83, 2895.97) * mm, "end": v(6910.83, 2895.97) * mm});
            skLineSegment(sketch, "E80.0.2.31", {"start": v(6982.83, 2894.97) * mm, "end": v(6910.83, 2894.97) * mm});
            skLineSegment(sketch, "E80.0.2.32", {"start": v(6216.83, 2858.97) * mm, "end": v(6148.83, 2894.97) * mm});
            skLineSegment(sketch, "E80.0.2.33", {"start": v(6148.83, 2894.97) * mm, "end": v(6076.83, 2894.97) * mm});
            skLineSegment(sketch, "E80.0.2.34", {"start": v(6564.83, 2858.97) * mm, "end": v(6494.83, 2858.97) * mm});
            skLineSegment(sketch, "E80.0.2.35", {"start": v(6704.83, 2894.97) * mm, "end": v(6632.83, 2894.97) * mm});
            skLineSegment(sketch, "E80.0.2.36", {"start": v(7120.83, 2858.97) * mm, "end": v(7050.83, 2858.97) * mm});
            skLineSegment(sketch, "E80.0.2.37", {"start": v(6354.83, 2894.97) * mm, "end": v(6286.83, 2858.97) * mm});
            skLineSegment(sketch, "E80.0.2.38", {"start": v(6772.83, 2859.97) * mm, "end": v(6704.83, 2895.97) * mm});
            skLineSegment(sketch, "E80.0.2.39", {"start": v(6632.83, 2894.97) * mm, "end": v(6564.83, 2858.97) * mm});
            skLineSegment(sketch, "E80.0.2.40", {"start": v(6426.83, 2895.97) * mm, "end": v(6354.83, 2895.97) * mm});
            skLineSegment(sketch, "E80.0.2.41", {"start": v(6494.83, 2859.97) * mm, "end": v(6426.83, 2895.97) * mm});
            skLineSegment(sketch, "E80.0.2.42", {"start": v(6704.83, 2895.97) * mm, "end": v(6632.83, 2895.97) * mm});
            skLineSegment(sketch, "E80.0.2.43", {"start": v(7120.83, 2859.97) * mm, "end": v(7050.83, 2859.97) * mm});
            skLineSegment(sketch, "E80.0.2.44", {"start": v(6772.83, 2858.97) * mm, "end": v(6704.83, 2894.97) * mm});
            skLineSegment(sketch, "E80.0.2.45", {"start": v(7050.83, 2858.97) * mm, "end": v(6982.83, 2894.97) * mm});
            skLineSegment(sketch, "E80.0.2.46", {"start": v(7188.83, 2894.97) * mm, "end": v(7120.83, 2858.97) * mm});
            skLineSegment(sketch, "E80.0.2.47", {"start": v(6426.83, 2894.97) * mm, "end": v(6354.83, 2894.97) * mm});
            skLineSegment(sketch, "E80.0.2.48", {"start": v(6842.83, 2858.97) * mm, "end": v(6772.83, 2858.97) * mm});
            skLineSegment(sketch, "E80.0.2.49", {"start": v(6286.83, 2858.97) * mm, "end": v(6216.83, 2858.97) * mm});
            skLineSegment(sketch, "E80.0.2.50", {"start": v(6842.83, 2859.97) * mm, "end": v(6772.83, 2859.97) * mm});
            skLineSegment(sketch, "E80.0.2.51", {"start": v(7188.83, 2895.97) * mm, "end": v(7120.83, 2859.97) * mm});
            skLineSegment(sketch, "E80.0.2.52", {"start": v(7050.83, 2859.97) * mm, "end": v(6982.83, 2895.97) * mm});
            skLineSegment(sketch, "E80.0.2.53", {"start": v(6286.83, 2859.97) * mm, "end": v(6216.83, 2859.97) * mm});
            skLineSegment(sketch, "E80.0.2.54", {"start": v(6564.83, 2859.97) * mm, "end": v(6494.83, 2859.97) * mm});
            skLineSegment(sketch, "E80.0.2.55", {"start": v(6354.83, 2895.97) * mm, "end": v(6286.83, 2859.97) * mm});
            skLineSegment(sketch, "E80.0.2.56", {"start": v(6632.83, 2895.97) * mm, "end": v(6564.83, 2859.97) * mm});
            skLineSegment(sketch, "E80.0.2.57", {"start": v(6494.83, 2858.97) * mm, "end": v(6426.83, 2894.97) * mm});
            skLineSegment(sketch, "E80.0.3.0", {"start": v(5520.83, 2895.97) * mm, "end": v(5452.83, 2859.97) * mm});
            skLineSegment(sketch, "E80.0.3.1", {"start": v(5520.83, 2894.97) * mm, "end": v(5452.83, 2858.97) * mm});
            skLineSegment(sketch, "E80.0.3.2", {"start": v(5592.83, 2895.97) * mm, "end": v(5520.83, 2895.97) * mm});
            skLineSegment(sketch, "E80.0.3.3", {"start": v(5870.83, 2895.97) * mm, "end": v(5798.83, 2895.97) * mm});
            skLineSegment(sketch, "E80.0.3.4", {"start": v(5660.83, 2858.97) * mm, "end": v(5592.83, 2894.97) * mm});
            skLineSegment(sketch, "E80.0.3.5", {"start": v(5730.83, 2858.97) * mm, "end": v(5660.83, 2858.97) * mm});
            skLineSegment(sketch, "E80.0.3.6", {"start": v(5382.83, 2858.97) * mm, "end": v(5314.83, 2894.97) * mm});
            skLineSegment(sketch, "E80.0.3.7", {"start": v(5798.83, 2894.97) * mm, "end": v(5730.83, 2858.97) * mm});
            skLineSegment(sketch, "E80.0.3.8", {"start": v(5382.83, 2859.97) * mm, "end": v(5314.83, 2895.97) * mm});
            skLineSegment(sketch, "E80.0.3.9", {"start": v(5730.83, 2859.97) * mm, "end": v(5660.83, 2859.97) * mm});
            skLineSegment(sketch, "E80.0.3.10", {"start": v(6008.83, 2858.97) * mm, "end": v(5938.83, 2858.97) * mm});
            skLineSegment(sketch, "E80.0.3.11", {"start": v(5452.83, 2859.97) * mm, "end": v(5382.83, 2859.97) * mm});
            skLineSegment(sketch, "E80.0.3.12", {"start": v(5592.83, 2894.97) * mm, "end": v(5520.83, 2894.97) * mm});
            skLineSegment(sketch, "E80.0.3.13", {"start": v(5938.83, 2858.97) * mm, "end": v(5870.83, 2894.97) * mm});
            skLineSegment(sketch, "E80.0.3.14", {"start": v(5938.83, 2859.97) * mm, "end": v(5870.83, 2895.97) * mm});
            skLineSegment(sketch, "E80.0.3.15", {"start": v(5314.83, 2895.97) * mm, "end": v(5242.83, 2895.97) * mm});
            skLineSegment(sketch, "E80.0.3.16", {"start": v(5798.83, 2895.97) * mm, "end": v(5730.83, 2859.97) * mm});
            skLineSegment(sketch, "E80.0.3.17", {"start": v(6008.83, 2859.97) * mm, "end": v(5938.83, 2859.97) * mm});
            skLineSegment(sketch, "E80.0.3.18", {"start": v(5870.83, 2894.97) * mm, "end": v(5798.83, 2894.97) * mm});
            skLineSegment(sketch, "E80.0.3.19", {"start": v(5660.83, 2859.97) * mm, "end": v(5592.83, 2895.97) * mm});
            skLineSegment(sketch, "E80.0.3.20", {"start": v(5314.83, 2894.97) * mm, "end": v(5242.83, 2894.97) * mm});
            skLineSegment(sketch, "E80.0.3.21", {"start": v(5452.83, 2858.97) * mm, "end": v(5382.83, 2858.97) * mm});
            skLineSegment(sketch, "E80.0.3.22", {"start": v(4548.83, 2859.97) * mm, "end": v(4270.83, 2859.97) * mm, "construction": true});
            skLineSegment(sketch, "E80.0.3.23", {"start": v(4130.83, 2895.97) * mm, "end": v(4062.83, 2859.97) * mm});
            skLineSegment(sketch, "E80.0.3.24", {"start": v(4130.83, 2894.97) * mm, "end": v(4062.83, 2858.97) * mm});
            skLineSegment(sketch, "E80.0.3.25", {"start": v(4548.83, 2858.97) * mm, "end": v(4270.83, 2858.97) * mm, "construction": true});
            skLineSegment(sketch, "E80.0.3.26", {"start": v(4964.83, 2894.97) * mm, "end": v(4896.83, 2858.97) * mm});
            skLineSegment(sketch, "E80.0.3.27", {"start": v(4964.83, 2895.97) * mm, "end": v(4896.83, 2859.97) * mm});
            skLineSegment(sketch, "E80.0.3.28", {"start": v(4202.83, 2895.97) * mm, "end": v(4130.83, 2895.97) * mm});
            skLineSegment(sketch, "E80.0.3.29", {"start": v(4270.83, 2859.97) * mm, "end": v(4202.83, 2895.97) * mm});
            skLineSegment(sketch, "E80.0.3.30", {"start": v(5036.83, 2895.97) * mm, "end": v(4964.83, 2895.97) * mm});
            skLineSegment(sketch, "E80.0.3.31", {"start": v(5036.83, 2894.97) * mm, "end": v(4964.83, 2894.97) * mm});
            skLineSegment(sketch, "E80.0.3.32", {"start": v(4270.83, 2858.97) * mm, "end": v(4202.83, 2894.97) * mm});
            skLineSegment(sketch, "E80.0.3.33", {"start": v(4202.83, 2894.97) * mm, "end": v(4130.83, 2894.97) * mm});
            skLineSegment(sketch, "E80.0.3.34", {"start": v(4618.83, 2858.97) * mm, "end": v(4548.83, 2858.97) * mm});
            skLineSegment(sketch, "E80.0.3.35", {"start": v(4758.83, 2894.97) * mm, "end": v(4686.83, 2894.97) * mm});
            skLineSegment(sketch, "E80.0.3.36", {"start": v(5174.83, 2858.97) * mm, "end": v(5104.83, 2858.97) * mm});
            skLineSegment(sketch, "E80.0.3.37", {"start": v(4408.83, 2894.97) * mm, "end": v(4340.83, 2858.97) * mm});
            skLineSegment(sketch, "E80.0.3.38", {"start": v(4826.83, 2859.97) * mm, "end": v(4758.83, 2895.97) * mm});
            skLineSegment(sketch, "E80.0.3.39", {"start": v(4686.83, 2894.97) * mm, "end": v(4618.83, 2858.97) * mm});
            skLineSegment(sketch, "E80.0.3.40", {"start": v(4480.83, 2895.97) * mm, "end": v(4408.83, 2895.97) * mm});
            skLineSegment(sketch, "E80.0.3.41", {"start": v(4548.83, 2859.97) * mm, "end": v(4480.83, 2895.97) * mm});
            skLineSegment(sketch, "E80.0.3.42", {"start": v(4758.83, 2895.97) * mm, "end": v(4686.83, 2895.97) * mm});
            skLineSegment(sketch, "E80.0.3.43", {"start": v(5174.83, 2859.97) * mm, "end": v(5104.83, 2859.97) * mm});
            skLineSegment(sketch, "E80.0.3.44", {"start": v(4826.83, 2858.97) * mm, "end": v(4758.83, 2894.97) * mm});
            skLineSegment(sketch, "E80.0.3.45", {"start": v(5104.83, 2858.97) * mm, "end": v(5036.83, 2894.97) * mm});
            skLineSegment(sketch, "E80.0.3.46", {"start": v(5242.83, 2894.97) * mm, "end": v(5174.83, 2858.97) * mm});
            skLineSegment(sketch, "E80.0.3.47", {"start": v(4480.83, 2894.97) * mm, "end": v(4408.83, 2894.97) * mm});
            skLineSegment(sketch, "E80.0.3.48", {"start": v(4896.83, 2858.97) * mm, "end": v(4826.83, 2858.97) * mm});
            skLineSegment(sketch, "E80.0.3.49", {"start": v(4340.83, 2858.97) * mm, "end": v(4270.83, 2858.97) * mm});
            skLineSegment(sketch, "E80.0.3.50", {"start": v(4896.83, 2859.97) * mm, "end": v(4826.83, 2859.97) * mm});
            skLineSegment(sketch, "E80.0.3.51", {"start": v(5242.83, 2895.97) * mm, "end": v(5174.83, 2859.97) * mm});
            skLineSegment(sketch, "E80.0.3.52", {"start": v(5104.83, 2859.97) * mm, "end": v(5036.83, 2895.97) * mm});
            skLineSegment(sketch, "E80.0.3.53", {"start": v(4340.83, 2859.97) * mm, "end": v(4270.83, 2859.97) * mm});
            skLineSegment(sketch, "E80.0.3.54", {"start": v(4618.83, 2859.97) * mm, "end": v(4548.83, 2859.97) * mm});
            skLineSegment(sketch, "E80.0.3.55", {"start": v(4408.83, 2895.97) * mm, "end": v(4340.83, 2859.97) * mm});
            skLineSegment(sketch, "E80.0.3.56", {"start": v(4686.83, 2895.97) * mm, "end": v(4618.83, 2859.97) * mm});
            skLineSegment(sketch, "E80.0.3.57", {"start": v(4548.83, 2858.97) * mm, "end": v(4480.83, 2894.97) * mm});
            skLineSegment(sketch, "E80.0.4.0", {"start": v(3574.83, 2895.97) * mm, "end": v(3506.83, 2859.97) * mm});
            skLineSegment(sketch, "E80.0.4.1", {"start": v(3574.83, 2894.97) * mm, "end": v(3506.83, 2858.97) * mm});
            skLineSegment(sketch, "E80.0.4.2", {"start": v(3646.83, 2895.97) * mm, "end": v(3574.83, 2895.97) * mm});
            skLineSegment(sketch, "E80.0.4.3", {"start": v(3924.83, 2895.97) * mm, "end": v(3852.83, 2895.97) * mm});
            skLineSegment(sketch, "E80.0.4.4", {"start": v(3714.83, 2858.97) * mm, "end": v(3646.83, 2894.97) * mm});
            skLineSegment(sketch, "E80.0.4.5", {"start": v(3784.83, 2858.97) * mm, "end": v(3714.83, 2858.97) * mm});
            skLineSegment(sketch, "E80.0.4.6", {"start": v(3436.83, 2858.97) * mm, "end": v(3368.83, 2894.97) * mm});
            skLineSegment(sketch, "E80.0.4.7", {"start": v(3852.83, 2894.97) * mm, "end": v(3784.83, 2858.97) * mm});
            skLineSegment(sketch, "E80.0.4.8", {"start": v(3436.83, 2859.97) * mm, "end": v(3368.83, 2895.97) * mm});
            skLineSegment(sketch, "E80.0.4.9", {"start": v(3784.83, 2859.97) * mm, "end": v(3714.83, 2859.97) * mm});
            skLineSegment(sketch, "E80.0.4.10", {"start": v(4062.83, 2858.97) * mm, "end": v(3992.83, 2858.97) * mm});
            skLineSegment(sketch, "E80.0.4.11", {"start": v(3506.83, 2859.97) * mm, "end": v(3436.83, 2859.97) * mm});
            skLineSegment(sketch, "E80.0.4.12", {"start": v(3646.83, 2894.97) * mm, "end": v(3574.83, 2894.97) * mm});
            skLineSegment(sketch, "E80.0.4.13", {"start": v(3992.83, 2858.97) * mm, "end": v(3924.83, 2894.97) * mm});
            skLineSegment(sketch, "E80.0.4.14", {"start": v(3992.83, 2859.97) * mm, "end": v(3924.83, 2895.97) * mm});
            skLineSegment(sketch, "E80.0.4.15", {"start": v(3368.83, 2895.97) * mm, "end": v(3296.83, 2895.97) * mm});
            skLineSegment(sketch, "E80.0.4.16", {"start": v(3852.83, 2895.97) * mm, "end": v(3784.83, 2859.97) * mm});
            skLineSegment(sketch, "E80.0.4.17", {"start": v(4062.83, 2859.97) * mm, "end": v(3992.83, 2859.97) * mm});
            skLineSegment(sketch, "E80.0.4.18", {"start": v(3924.83, 2894.97) * mm, "end": v(3852.83, 2894.97) * mm});
            skLineSegment(sketch, "E80.0.4.19", {"start": v(3714.83, 2859.97) * mm, "end": v(3646.83, 2895.97) * mm});
            skLineSegment(sketch, "E80.0.4.20", {"start": v(3368.83, 2894.97) * mm, "end": v(3296.83, 2894.97) * mm});
            skLineSegment(sketch, "E80.0.4.21", {"start": v(3506.83, 2858.97) * mm, "end": v(3436.83, 2858.97) * mm});
            skLineSegment(sketch, "E80.0.4.22", {"start": v(2602.83, 2859.97) * mm, "end": v(2324.83, 2859.97) * mm, "construction": true});
            skLineSegment(sketch, "E80.0.4.23", {"start": v(2184.83, 2895.97) * mm, "end": v(2116.83, 2859.97) * mm});
            skLineSegment(sketch, "E80.0.4.24", {"start": v(2184.83, 2894.97) * mm, "end": v(2116.83, 2858.97) * mm});
            skLineSegment(sketch, "E80.0.4.25", {"start": v(2602.83, 2858.97) * mm, "end": v(2324.83, 2858.97) * mm, "construction": true});
            skLineSegment(sketch, "E80.0.4.26", {"start": v(3018.83, 2894.97) * mm, "end": v(2950.83, 2858.97) * mm});
            skLineSegment(sketch, "E80.0.4.27", {"start": v(3018.83, 2895.97) * mm, "end": v(2950.83, 2859.97) * mm});
            skLineSegment(sketch, "E80.0.4.28", {"start": v(2256.83, 2895.97) * mm, "end": v(2184.83, 2895.97) * mm});
            skLineSegment(sketch, "E80.0.4.29", {"start": v(2324.83, 2859.97) * mm, "end": v(2256.83, 2895.97) * mm});
            skLineSegment(sketch, "E80.0.4.30", {"start": v(3090.83, 2895.97) * mm, "end": v(3018.83, 2895.97) * mm});
            skLineSegment(sketch, "E80.0.4.31", {"start": v(3090.83, 2894.97) * mm, "end": v(3018.83, 2894.97) * mm});
            skLineSegment(sketch, "E80.0.4.32", {"start": v(2324.83, 2858.97) * mm, "end": v(2256.83, 2894.97) * mm});
            skLineSegment(sketch, "E80.0.4.33", {"start": v(2256.83, 2894.97) * mm, "end": v(2184.83, 2894.97) * mm});
            skLineSegment(sketch, "E80.0.4.34", {"start": v(2672.83, 2858.97) * mm, "end": v(2602.83, 2858.97) * mm});
            skLineSegment(sketch, "E80.0.4.35", {"start": v(2812.83, 2894.97) * mm, "end": v(2740.83, 2894.97) * mm});
            skLineSegment(sketch, "E80.0.4.36", {"start": v(3228.83, 2858.97) * mm, "end": v(3158.83, 2858.97) * mm});
            skLineSegment(sketch, "E80.0.4.37", {"start": v(2462.83, 2894.97) * mm, "end": v(2394.83, 2858.97) * mm});
            skLineSegment(sketch, "E80.0.4.38", {"start": v(2880.83, 2859.97) * mm, "end": v(2812.83, 2895.97) * mm});
            skLineSegment(sketch, "E80.0.4.39", {"start": v(2740.83, 2894.97) * mm, "end": v(2672.83, 2858.97) * mm});
            skLineSegment(sketch, "E80.0.4.40", {"start": v(2534.83, 2895.97) * mm, "end": v(2462.83, 2895.97) * mm});
            skLineSegment(sketch, "E80.0.4.41", {"start": v(2602.83, 2859.97) * mm, "end": v(2534.83, 2895.97) * mm});
            skLineSegment(sketch, "E80.0.4.42", {"start": v(2812.83, 2895.97) * mm, "end": v(2740.83, 2895.97) * mm});
            skLineSegment(sketch, "E80.0.4.43", {"start": v(3228.83, 2859.97) * mm, "end": v(3158.83, 2859.97) * mm});
            skLineSegment(sketch, "E80.0.4.44", {"start": v(2880.83, 2858.97) * mm, "end": v(2812.83, 2894.97) * mm});
            skLineSegment(sketch, "E80.0.4.45", {"start": v(3158.83, 2858.97) * mm, "end": v(3090.83, 2894.97) * mm});
            skLineSegment(sketch, "E80.0.4.46", {"start": v(3296.83, 2894.97) * mm, "end": v(3228.83, 2858.97) * mm});
            skLineSegment(sketch, "E80.0.4.47", {"start": v(2534.83, 2894.97) * mm, "end": v(2462.83, 2894.97) * mm});
            skLineSegment(sketch, "E80.0.4.48", {"start": v(2950.83, 2858.97) * mm, "end": v(2880.83, 2858.97) * mm});
            skLineSegment(sketch, "E80.0.4.49", {"start": v(2394.83, 2858.97) * mm, "end": v(2324.83, 2858.97) * mm});
            skLineSegment(sketch, "E80.0.4.50", {"start": v(2950.83, 2859.97) * mm, "end": v(2880.83, 2859.97) * mm});
            skLineSegment(sketch, "E80.0.4.51", {"start": v(3296.83, 2895.97) * mm, "end": v(3228.83, 2859.97) * mm});
            skLineSegment(sketch, "E80.0.4.52", {"start": v(3158.83, 2859.97) * mm, "end": v(3090.83, 2895.97) * mm});
            skLineSegment(sketch, "E80.0.4.53", {"start": v(2394.83, 2859.97) * mm, "end": v(2324.83, 2859.97) * mm});
            skLineSegment(sketch, "E80.0.4.54", {"start": v(2672.83, 2859.97) * mm, "end": v(2602.83, 2859.97) * mm});
            skLineSegment(sketch, "E80.0.4.55", {"start": v(2462.83, 2895.97) * mm, "end": v(2394.83, 2859.97) * mm});
            skLineSegment(sketch, "E80.0.4.56", {"start": v(2740.83, 2895.97) * mm, "end": v(2672.83, 2859.97) * mm});
            skLineSegment(sketch, "E80.0.4.57", {"start": v(2602.83, 2858.97) * mm, "end": v(2534.83, 2894.97) * mm});
            skLineSegment(sketch, "E80.0.5.0", {"start": v(1628.83, 2895.97) * mm, "end": v(1560.83, 2859.97) * mm});
            skLineSegment(sketch, "E80.0.5.1", {"start": v(1628.83, 2894.97) * mm, "end": v(1560.83, 2858.97) * mm});
            skLineSegment(sketch, "E80.0.5.2", {"start": v(1700.83, 2895.97) * mm, "end": v(1628.83, 2895.97) * mm});
            skLineSegment(sketch, "E80.0.5.3", {"start": v(1978.83, 2895.97) * mm, "end": v(1906.83, 2895.97) * mm});
            skLineSegment(sketch, "E80.0.5.4", {"start": v(1768.83, 2858.97) * mm, "end": v(1700.83, 2894.97) * mm});
            skLineSegment(sketch, "E80.0.5.5", {"start": v(1838.83, 2858.97) * mm, "end": v(1768.83, 2858.97) * mm});
            skLineSegment(sketch, "E80.0.5.6", {"start": v(1490.83, 2858.97) * mm, "end": v(1422.83, 2894.97) * mm});
            skLineSegment(sketch, "E80.0.5.7", {"start": v(1906.83, 2894.97) * mm, "end": v(1838.83, 2858.97) * mm});
            skLineSegment(sketch, "E80.0.5.8", {"start": v(1490.83, 2859.97) * mm, "end": v(1422.83, 2895.97) * mm});
            skLineSegment(sketch, "E80.0.5.9", {"start": v(1838.83, 2859.97) * mm, "end": v(1768.83, 2859.97) * mm});
            skLineSegment(sketch, "E80.0.5.10", {"start": v(2116.83, 2858.97) * mm, "end": v(2046.83, 2858.97) * mm});
            skLineSegment(sketch, "E80.0.5.11", {"start": v(1560.83, 2859.97) * mm, "end": v(1490.83, 2859.97) * mm});
            skLineSegment(sketch, "E80.0.5.12", {"start": v(1700.83, 2894.97) * mm, "end": v(1628.83, 2894.97) * mm});
            skLineSegment(sketch, "E80.0.5.13", {"start": v(2046.83, 2858.97) * mm, "end": v(1978.83, 2894.97) * mm});
            skLineSegment(sketch, "E80.0.5.14", {"start": v(2046.83, 2859.97) * mm, "end": v(1978.83, 2895.97) * mm});
            skLineSegment(sketch, "E80.0.5.15", {"start": v(1422.83, 2895.97) * mm, "end": v(1350.83, 2895.97) * mm});
            skLineSegment(sketch, "E80.0.5.16", {"start": v(1906.83, 2895.97) * mm, "end": v(1838.83, 2859.97) * mm});
            skLineSegment(sketch, "E80.0.5.17", {"start": v(2116.83, 2859.97) * mm, "end": v(2046.83, 2859.97) * mm});
            skLineSegment(sketch, "E80.0.5.18", {"start": v(1978.83, 2894.97) * mm, "end": v(1906.83, 2894.97) * mm});
            skLineSegment(sketch, "E80.0.5.19", {"start": v(1768.83, 2859.97) * mm, "end": v(1700.83, 2895.97) * mm});
            skLineSegment(sketch, "E80.0.5.20", {"start": v(1422.83, 2894.97) * mm, "end": v(1350.83, 2894.97) * mm});
            skLineSegment(sketch, "E80.0.5.21", {"start": v(1560.83, 2858.97) * mm, "end": v(1490.83, 2858.97) * mm});
            skLineSegment(sketch, "E80.0.5.22", {"start": v(656.83, 2859.97) * mm, "end": v(378.83, 2859.97) * mm, "construction": true});
            skLineSegment(sketch, "E80.0.5.23", {"start": v(238.83, 2895.97) * mm, "end": v(170.83, 2859.97) * mm});
            skLineSegment(sketch, "E80.0.5.24", {"start": v(238.83, 2894.97) * mm, "end": v(170.83, 2858.97) * mm});
            skLineSegment(sketch, "E80.0.5.25", {"start": v(656.83, 2858.97) * mm, "end": v(378.83, 2858.97) * mm, "construction": true});
            skLineSegment(sketch, "E80.0.5.26", {"start": v(1072.83, 2894.97) * mm, "end": v(1004.83, 2858.97) * mm});
            skLineSegment(sketch, "E80.0.5.27", {"start": v(1072.83, 2895.97) * mm, "end": v(1004.83, 2859.97) * mm});
            skLineSegment(sketch, "E80.0.5.28", {"start": v(310.83, 2895.97) * mm, "end": v(238.83, 2895.97) * mm});
            skLineSegment(sketch, "E80.0.5.29", {"start": v(378.83, 2859.97) * mm, "end": v(310.83, 2895.97) * mm});
            skLineSegment(sketch, "E80.0.5.30", {"start": v(1144.83, 2895.97) * mm, "end": v(1072.83, 2895.97) * mm});
            skLineSegment(sketch, "E80.0.5.31", {"start": v(1144.83, 2894.97) * mm, "end": v(1072.83, 2894.97) * mm});
            skLineSegment(sketch, "E80.0.5.32", {"start": v(378.83, 2858.97) * mm, "end": v(310.83, 2894.97) * mm});
            skLineSegment(sketch, "E80.0.5.33", {"start": v(310.83, 2894.97) * mm, "end": v(238.83, 2894.97) * mm});
            skLineSegment(sketch, "E80.0.5.34", {"start": v(726.83, 2858.97) * mm, "end": v(656.83, 2858.97) * mm});
            skLineSegment(sketch, "E80.0.5.35", {"start": v(866.83, 2894.97) * mm, "end": v(794.83, 2894.97) * mm});
            skLineSegment(sketch, "E80.0.5.36", {"start": v(1282.83, 2858.97) * mm, "end": v(1212.83, 2858.97) * mm});
            skLineSegment(sketch, "E80.0.5.37", {"start": v(516.83, 2894.97) * mm, "end": v(448.83, 2858.97) * mm});
            skLineSegment(sketch, "E80.0.5.38", {"start": v(934.83, 2859.97) * mm, "end": v(866.83, 2895.97) * mm});
            skLineSegment(sketch, "E80.0.5.39", {"start": v(794.83, 2894.97) * mm, "end": v(726.83, 2858.97) * mm});
            skLineSegment(sketch, "E80.0.5.40", {"start": v(588.83, 2895.97) * mm, "end": v(516.83, 2895.97) * mm});
            skLineSegment(sketch, "E80.0.5.41", {"start": v(656.83, 2859.97) * mm, "end": v(588.83, 2895.97) * mm});
            skLineSegment(sketch, "E80.0.5.42", {"start": v(866.83, 2895.97) * mm, "end": v(794.83, 2895.97) * mm});
            skLineSegment(sketch, "E80.0.5.43", {"start": v(1282.83, 2859.97) * mm, "end": v(1212.83, 2859.97) * mm});
            skLineSegment(sketch, "E80.0.5.44", {"start": v(934.83, 2858.97) * mm, "end": v(866.83, 2894.97) * mm});
            skLineSegment(sketch, "E80.0.5.45", {"start": v(1212.83, 2858.97) * mm, "end": v(1144.83, 2894.97) * mm});
            skLineSegment(sketch, "E80.0.5.46", {"start": v(1350.83, 2894.97) * mm, "end": v(1282.83, 2858.97) * mm});
            skLineSegment(sketch, "E80.0.5.47", {"start": v(588.83, 2894.97) * mm, "end": v(516.83, 2894.97) * mm});
            skLineSegment(sketch, "E80.0.5.48", {"start": v(1004.83, 2858.97) * mm, "end": v(934.83, 2858.97) * mm});
            skLineSegment(sketch, "E80.0.5.49", {"start": v(448.83, 2858.97) * mm, "end": v(378.83, 2858.97) * mm});
            skLineSegment(sketch, "E80.0.5.50", {"start": v(1004.83, 2859.97) * mm, "end": v(934.83, 2859.97) * mm});
            skLineSegment(sketch, "E80.0.5.51", {"start": v(1350.83, 2895.97) * mm, "end": v(1282.83, 2859.97) * mm});
            skLineSegment(sketch, "E80.0.5.52", {"start": v(1212.83, 2859.97) * mm, "end": v(1144.83, 2895.97) * mm});
            skLineSegment(sketch, "E80.0.5.53", {"start": v(448.83, 2859.97) * mm, "end": v(378.83, 2859.97) * mm});
            skLineSegment(sketch, "E80.0.5.54", {"start": v(726.83, 2859.97) * mm, "end": v(656.83, 2859.97) * mm});
            skLineSegment(sketch, "E80.0.5.55", {"start": v(516.83, 2895.97) * mm, "end": v(448.83, 2859.97) * mm});
            skLineSegment(sketch, "E80.0.5.56", {"start": v(794.83, 2895.97) * mm, "end": v(726.83, 2859.97) * mm});
            skLineSegment(sketch, "E80.0.5.57", {"start": v(656.83, 2858.97) * mm, "end": v(588.83, 2894.97) * mm});
            skLineSegment(sketch, "E80.direction1", {"start": v(11846.83, 2858.97) * mm, "end": v(11846.83, 2883.97) * mm, "construction": true});
            skLineSegment(sketch, "E80.direction2", {"start": v(11846.83, 2858.97) * mm, "end": v(9900.83, 2858.97) * mm, "construction": true});
            skLineSegment(sketch, "E81", {"start": v(170.83, 2859.97) * mm, "end": v(100, 2859.97) * mm});
            skLineSegment(sketch, "E82", {"start": v(100, 2859.97) * mm, "end": v(100, 2858.97) * mm});
            skLineSegment(sketch, "E83", {"start": v(100, 2858.97) * mm, "end": v(170.83, 2858.97) * mm});
            skSolve(sketch);
        }
        {
            var Q0;
            Q0 = qSketchRegion(id + "F16", true);
            extrude(context, id + "F17", {"entities" : qUnion([Q0]), "operationType" : NewBodyOperationType.ADD, "depth" : 2236 * mm, "offsetDistance" : 25 * mm});
        }
    });
